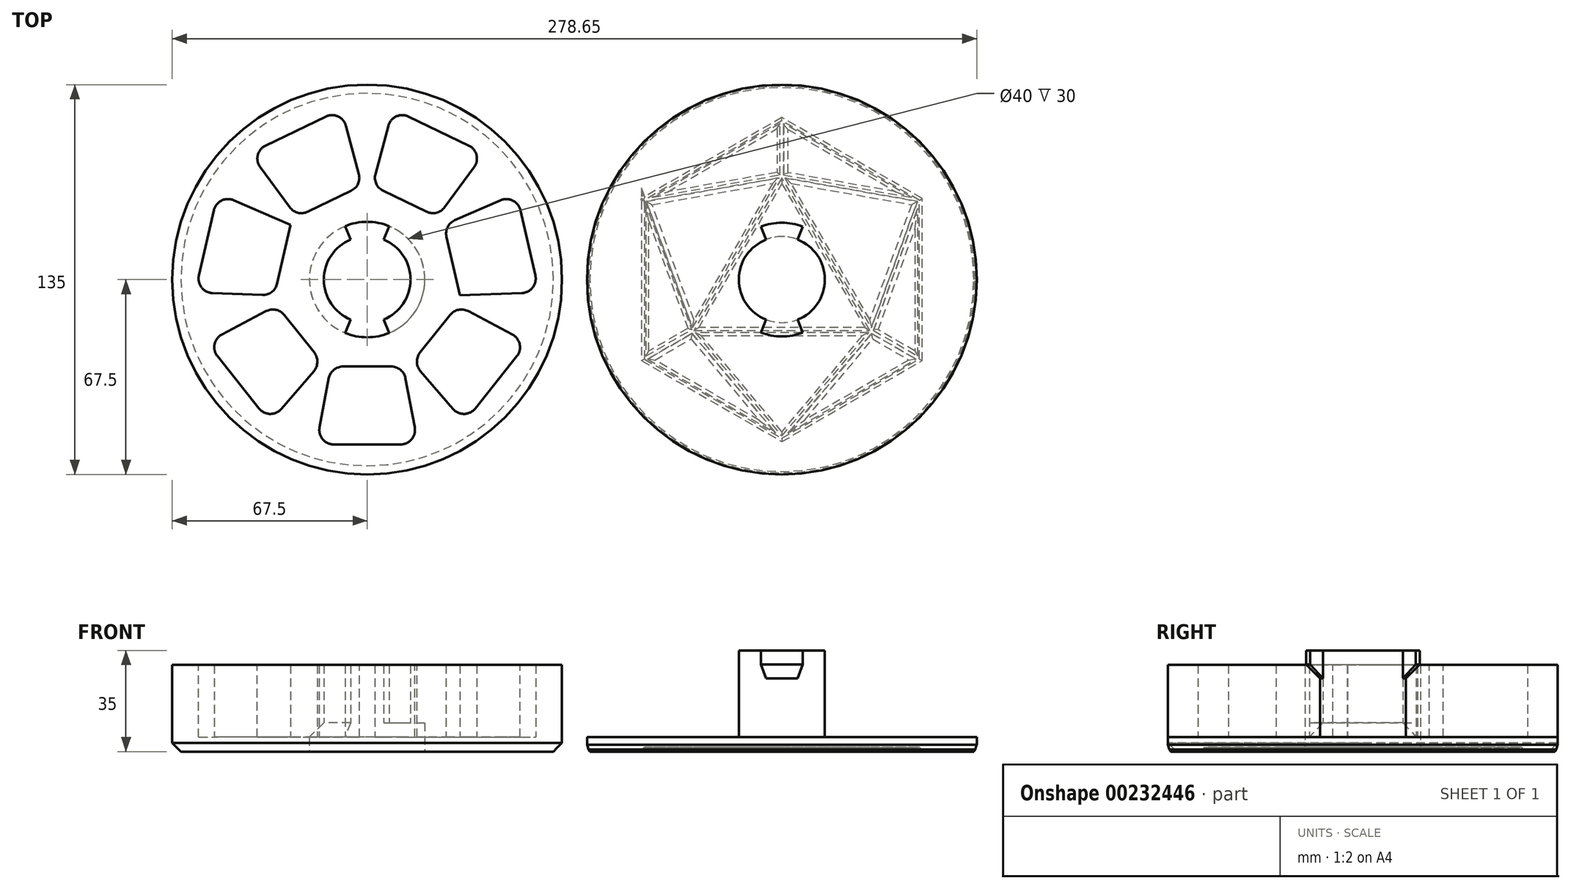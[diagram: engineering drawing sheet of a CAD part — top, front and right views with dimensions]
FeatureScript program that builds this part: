
annotation { "Feature Type Name" : "Feature", "Feature Type Description" : "" }
export const myFeature = defineFeature(function(context is Context, id is Id, definition is map)
    precondition{}
    {
        {
            var Q0;
            Q0=qCreatedBy(makeId("Top.planeOp"),FACE);
            var sketch = newSketch(context, id + "F0", { "sketchPlane" : qUnion([Q0])});
            skCircle(sketch, "E0.cCircle", {"center": v(0, 0) * mm, "radius": 63.39 * mm, "construction": true});
            skLineSegment(sketch, "E0.0", {"start": v(0, 63.39) * mm, "end": v(49.56, 39.52) * mm});
            skLineSegment(sketch, "E0.1", {"start": v(49.56, 39.52) * mm, "end": v(61.8, -14.1) * mm});
            skLineSegment(sketch, "E0.2", {"start": v(61.8, -14.1) * mm, "end": v(27.5, -57.1) * mm});
            skLineSegment(sketch, "E0.3", {"start": v(27.5, -57.1) * mm, "end": v(-27.5, -57.1) * mm});
            skLineSegment(sketch, "E0.4", {"start": v(-27.5, -57.1) * mm, "end": v(-61.8, -14.1) * mm});
            skLineSegment(sketch, "E0.5", {"start": v(-61.8, -14.1) * mm, "end": v(-49.56, 39.52) * mm});
            skLineSegment(sketch, "E0.6", {"start": v(-49.56, 39.52) * mm, "end": v(0, 63.39) * mm});
            skCircle(sketch, "E1.cCircle", {"center": v(0, 0) * mm, "radius": 33.42 * mm, "construction": true});
            skLineSegment(sketch, "E1.0", {"start": v(0, 33.42) * mm, "end": v(26.13, 20.84) * mm});
            skLineSegment(sketch, "E1.1", {"start": v(26.13, 20.84) * mm, "end": v(32.58, -7.44) * mm});
            skLineSegment(sketch, "E1.2", {"start": v(32.58, -7.44) * mm, "end": v(14.5, -30.1) * mm});
            skLineSegment(sketch, "E1.3", {"start": v(14.5, -30.1) * mm, "end": v(-14.5, -30.1) * mm});
            skLineSegment(sketch, "E1.4", {"start": v(-14.5, -30.1) * mm, "end": v(-32.58, -7.44) * mm});
            skLineSegment(sketch, "E1.5", {"start": v(-32.58, -7.44) * mm, "end": v(-26.13, 20.84) * mm});
            skLineSegment(sketch, "E1.6", {"start": v(-26.13, 20.84) * mm, "end": v(0, 33.42) * mm});
            skCircle(sketch, "E2", {"center": v(0, 0) * mm, "radius": 67.5 * mm});
            skCircle(sketch, "E3", {"center": v(0, 0) * mm, "radius": 15 * mm});
            skLineSegment(sketch, "E4", {"start": v(-26.13, 20.84) * mm, "end": v(-49.56, 39.52) * mm});
            skLineSegment(sketch, "E5", {"start": v(0, 33.42) * mm, "end": v(0, 63.39) * mm});
            skLineSegment(sketch, "E6", {"start": v(26.13, 20.84) * mm, "end": v(49.56, 39.52) * mm});
            skLineSegment(sketch, "E7", {"start": v(32.58, -7.44) * mm, "end": v(61.8, -14.1) * mm});
            skLineSegment(sketch, "E8", {"start": v(14.5, -30.1) * mm, "end": v(27.5, -57.1) * mm});
            skLineSegment(sketch, "E9", {"start": v(-14.5, -30.1) * mm, "end": v(-27.5, -57.1) * mm});
            skLineSegment(sketch, "E10", {"start": v(-61.8, -14.1) * mm, "end": v(-32.58, -7.44) * mm});
            skLineSegment(sketch, "E11", {"start": v(-26.57, 18.89) * mm, "end": v(-51.76, 29.88) * mm});
            skLineSegment(sketch, "E12", {"start": v(-24.33, 21.7) * mm, "end": v(-40.64, 43.81) * mm});
            skLineSegment(sketch, "E13", {"start": v(-1.8, 32.55) * mm, "end": v(-8.91, 59.1) * mm});
            skLineSegment(sketch, "E14", {"start": v(1.8, 32.55) * mm, "end": v(8.91, 59.1) * mm});
            skLineSegment(sketch, "E15", {"start": v(26.57, 18.89) * mm, "end": v(51.76, 29.88) * mm});
            skLineSegment(sketch, "E16", {"start": v(24.33, 21.7) * mm, "end": v(40.64, 43.81) * mm});
            skLineSegment(sketch, "E17", {"start": v(31.33, -9) * mm, "end": v(55.63, -21.84) * mm});
            skLineSegment(sketch, "E18", {"start": v(32.14, -5.49) * mm, "end": v(59.6, -4.46) * mm});
            skLineSegment(sketch, "E19", {"start": v(15.75, -28.55) * mm, "end": v(33.67, -49.37) * mm});
            skLineSegment(sketch, "E20", {"start": v(12.5, -30.1) * mm, "end": v(17.6, -57.1) * mm});
            skLineSegment(sketch, "E21", {"start": v(-12.5, -30.1) * mm, "end": v(-17.6, -57.1) * mm});
            skLineSegment(sketch, "E22", {"start": v(-15.75, -28.55) * mm, "end": v(-33.67, -49.37) * mm});
            skLineSegment(sketch, "E23", {"start": v(-31.33, -9) * mm, "end": v(-55.63, -21.84) * mm});
            skLineSegment(sketch, "E24", {"start": v(-32.14, -5.49) * mm, "end": v(-59.6, -4.46) * mm});
            skLineSegment(sketch, "E25", {"start": v(67.5, 0) * mm, "end": v(143.65, 0) * mm});
            skCircle(sketch, "E26", {"center": v(143.65, 0) * mm, "radius": 67.5 * mm});
            skCircle(sketch, "E27", {"center": v(0, 0) * mm, "radius": 20 * mm});
            skLineSegment(sketch, "E28", {"start": v(0, 0) * mm, "end": v(-7.65, 18.48) * mm});
            skLineSegment(sketch, "E29", {"start": v(0, 0) * mm, "end": v(7.65, 18.48) * mm});
            skLineSegment(sketch, "E30", {"start": v(0, 0) * mm, "end": v(-7.65, -18.48) * mm});
            skLineSegment(sketch, "E31", {"start": v(0, 0) * mm, "end": v(7.65, -18.48) * mm});
            skSolve(sketch);
        }
        {
            var Q0;
            {var subQ0=sQuery(id+"F0.wireOp",EDGE,"E28");var subQ1=sQuery(id+"F0.wireOp",EDGE,"E3");var subQ2=makeQuery(id+"F0.imprint","INTERSECT",VERTEX,{"derivedFrom":[subQ1,subQ0]});Q0=makeQuery(id+"F0.imprint","IMPRINT",FACE,{"disambiguationData":[TD([[makeQuery(id+"F0.imprint","IMPRINT",EDGE,{"disambiguationData":[TD([[subQ2,-1.0]])],"derivedFrom":subQ1}),-1.0]])]});}
            var Q1;
            {var subQ0=sQuery(id+"F0.wireOp",EDGE,"E29");var subQ1=sQuery(id+"F0.wireOp",EDGE,"E3");var subQ2=makeQuery(id+"F0.imprint","INTERSECT",VERTEX,{"derivedFrom":[subQ1,subQ0]});Q1=makeQuery(id+"F0.imprint","IMPRINT",FACE,{"disambiguationData":[TD([[makeQuery(id+"F0.imprint","IMPRINT",EDGE,{"disambiguationData":[TD([[subQ2,1.0]])],"derivedFrom":subQ1}),-1.0]])]});}
            var Q2;
            {var subQ0=sQuery(id+"F0.wireOp",EDGE,"E4");Q2=makeQuery(id+"F0.imprint","IMPRINT",FACE,{"disambiguationData":[TD([[makeQuery(id+"F0.imprint","IMPRINT",EDGE,{"derivedFrom":subQ0}),1.0]])]});}
            var Q3;
            {var subQ0=sQuery(id+"F0.wireOp",EDGE,"E4");Q3=makeQuery(id+"F0.imprint","IMPRINT",FACE,{"disambiguationData":[TD([[makeQuery(id+"F0.imprint","IMPRINT",EDGE,{"derivedFrom":subQ0}),-1.0]])]});}
            var Q4;
            Q4=makeQuery(id+"F0.imprint","IMPRINT",FACE,{"disambiguationData":[TD([[makeQuery(id+"F0.imprint","IMPRINT",EDGE,{"derivedFrom":sQuery(id+"F0.wireOp",EDGE,"E2")}),1.0]])]});
            var Q5;
            {var subQ0=sQuery(id+"F0.wireOp",EDGE,"E5");Q5=makeQuery(id+"F0.imprint","IMPRINT",FACE,{"disambiguationData":[TD([[makeQuery(id+"F0.imprint","IMPRINT",EDGE,{"derivedFrom":subQ0}),-1.0]])]});}
            var Q6;
            {var subQ0=sQuery(id+"F0.wireOp",EDGE,"E5");Q6=makeQuery(id+"F0.imprint","IMPRINT",FACE,{"disambiguationData":[TD([[makeQuery(id+"F0.imprint","IMPRINT",EDGE,{"derivedFrom":subQ0}),1.0]])]});}
            var Q7;
            {var subQ0=sQuery(id+"F0.wireOp",EDGE,"E6");Q7=makeQuery(id+"F0.imprint","IMPRINT",FACE,{"disambiguationData":[TD([[makeQuery(id+"F0.imprint","IMPRINT",EDGE,{"derivedFrom":subQ0}),1.0]])]});}
            var Q8;
            {var subQ0=sQuery(id+"F0.wireOp",EDGE,"E6");Q8=makeQuery(id+"F0.imprint","IMPRINT",FACE,{"disambiguationData":[TD([[makeQuery(id+"F0.imprint","IMPRINT",EDGE,{"derivedFrom":subQ0}),-1.0]])]});}
            var Q9;
            {var subQ0=sQuery(id+"F0.wireOp",EDGE,"E7");Q9=makeQuery(id+"F0.imprint","IMPRINT",FACE,{"disambiguationData":[TD([[makeQuery(id+"F0.imprint","IMPRINT",EDGE,{"derivedFrom":subQ0}),1.0]])]});}
            var Q10;
            {var subQ0=sQuery(id+"F0.wireOp",EDGE,"E7");Q10=makeQuery(id+"F0.imprint","IMPRINT",FACE,{"disambiguationData":[TD([[makeQuery(id+"F0.imprint","IMPRINT",EDGE,{"derivedFrom":subQ0}),-1.0]])]});}
            var Q11;
            {var subQ0=sQuery(id+"F0.wireOp",EDGE,"E8");Q11=makeQuery(id+"F0.imprint","IMPRINT",FACE,{"disambiguationData":[TD([[makeQuery(id+"F0.imprint","IMPRINT",EDGE,{"derivedFrom":subQ0}),1.0]])]});}
            var Q12;
            {var subQ0=sQuery(id+"F0.wireOp",EDGE,"E8");Q12=makeQuery(id+"F0.imprint","IMPRINT",FACE,{"disambiguationData":[TD([[makeQuery(id+"F0.imprint","IMPRINT",EDGE,{"derivedFrom":subQ0}),-1.0]])]});}
            var Q13;
            {var subQ0=sQuery(id+"F0.wireOp",EDGE,"E9");Q13=makeQuery(id+"F0.imprint","IMPRINT",FACE,{"disambiguationData":[TD([[makeQuery(id+"F0.imprint","IMPRINT",EDGE,{"derivedFrom":subQ0}),1.0]])]});}
            var Q14;
            {var subQ0=sQuery(id+"F0.wireOp",EDGE,"E9");Q14=makeQuery(id+"F0.imprint","IMPRINT",FACE,{"disambiguationData":[TD([[makeQuery(id+"F0.imprint","IMPRINT",EDGE,{"derivedFrom":subQ0}),-1.0]])]});}
            var Q15;
            {var subQ0=sQuery(id+"F0.wireOp",EDGE,"E10");Q15=makeQuery(id+"F0.imprint","IMPRINT",FACE,{"disambiguationData":[TD([[makeQuery(id+"F0.imprint","IMPRINT",EDGE,{"derivedFrom":subQ0}),-1.0]])]});}
            var Q16;
            {var subQ0=sQuery(id+"F0.wireOp",EDGE,"E10");Q16=makeQuery(id+"F0.imprint","IMPRINT",FACE,{"disambiguationData":[TD([[makeQuery(id+"F0.imprint","IMPRINT",EDGE,{"derivedFrom":subQ0}),1.0]])]});}
            var Q17;
            {var subQ1=sQuery(id+"F0.wireOp",EDGE,"E1.0");var subQ21=makeQuery(id+"F0.imprint","INTERSECT",VERTEX,{"derivedFrom":[subQ1,sQuery(id+"F0.wireOp",EDGE,"E14")]});Q17=makeQuery(id+"F0.imprint","IMPRINT",FACE,{"disambiguationData":[TD([[makeQuery(id+"F0.imprint","IMPRINT",EDGE,{"disambiguationData":[TD([[subQ21,-1.0]])],"derivedFrom":subQ1}),-1.0]])]});}
            extrude(context, id + "F1", {"entities" : qUnion([Q0, Q1, Q2, Q3, Q4, Q5, Q6, Q7, Q8, Q9, Q10, Q11, Q12, Q13, Q14, Q15, Q16, Q17]), "depth" : 25 * mm});
        }
        {
            var Q0;
            {var subQ0=sQuery(id+"F0.wireOp",EDGE,"E5");Q0=makeQuery(id+"F0.imprint","IMPRINT",FACE,{"disambiguationData":[TD([[makeQuery(id+"F0.imprint","IMPRINT",EDGE,{"derivedFrom":subQ0}),-1.0]])]});}
            var Q1;
            {var subQ0=sQuery(id+"F0.wireOp",EDGE,"E5");Q1=makeQuery(id+"F0.imprint","IMPRINT",FACE,{"disambiguationData":[TD([[makeQuery(id+"F0.imprint","IMPRINT",EDGE,{"derivedFrom":subQ0}),1.0]])]});}
            var Q2;
            {var subQ0=sQuery(id+"F0.wireOp",EDGE,"E4");Q2=makeQuery(id+"F0.imprint","IMPRINT",FACE,{"disambiguationData":[TD([[makeQuery(id+"F0.imprint","IMPRINT",EDGE,{"derivedFrom":subQ0}),-1.0]])]});}
            var Q3;
            {var subQ0=sQuery(id+"F0.wireOp",EDGE,"E4");Q3=makeQuery(id+"F0.imprint","IMPRINT",FACE,{"disambiguationData":[TD([[makeQuery(id+"F0.imprint","IMPRINT",EDGE,{"derivedFrom":subQ0}),1.0]])]});}
            var Q4;
            {var subQ0=sQuery(id+"F0.wireOp",EDGE,"E22");Q4=makeQuery(id+"F0.imprint","IMPRINT",FACE,{"disambiguationData":[TD([[makeQuery(id+"F0.imprint","IMPRINT",EDGE,{"derivedFrom":subQ0}),-1.0]])]});}
            var Q5;
            {var subQ0=sQuery(id+"F0.wireOp",EDGE,"E9");Q5=makeQuery(id+"F0.imprint","IMPRINT",FACE,{"disambiguationData":[TD([[makeQuery(id+"F0.imprint","IMPRINT",EDGE,{"derivedFrom":subQ0}),-1.0]])]});}
            var Q6;
            {var subQ0=sQuery(id+"F0.wireOp",EDGE,"E9");Q6=makeQuery(id+"F0.imprint","IMPRINT",FACE,{"disambiguationData":[TD([[makeQuery(id+"F0.imprint","IMPRINT",EDGE,{"derivedFrom":subQ0}),1.0]])]});}
            var Q7;
            {var subQ0=sQuery(id+"F0.wireOp",EDGE,"E20");Q7=makeQuery(id+"F0.imprint","IMPRINT",FACE,{"disambiguationData":[TD([[makeQuery(id+"F0.imprint","IMPRINT",EDGE,{"derivedFrom":subQ0}),-1.0]])]});}
            var Q8;
            {var subQ0=sQuery(id+"F0.wireOp",EDGE,"E8");Q8=makeQuery(id+"F0.imprint","IMPRINT",FACE,{"disambiguationData":[TD([[makeQuery(id+"F0.imprint","IMPRINT",EDGE,{"derivedFrom":subQ0}),-1.0]])]});}
            var Q9;
            {var subQ0=sQuery(id+"F0.wireOp",EDGE,"E8");Q9=makeQuery(id+"F0.imprint","IMPRINT",FACE,{"disambiguationData":[TD([[makeQuery(id+"F0.imprint","IMPRINT",EDGE,{"derivedFrom":subQ0}),1.0]])]});}
            var Q10;
            {var subQ0=sQuery(id+"F0.wireOp",EDGE,"E17");Q10=makeQuery(id+"F0.imprint","IMPRINT",FACE,{"disambiguationData":[TD([[makeQuery(id+"F0.imprint","IMPRINT",EDGE,{"derivedFrom":subQ0}),-1.0]])]});}
            var Q11;
            {var subQ0=sQuery(id+"F0.wireOp",EDGE,"E7");Q11=makeQuery(id+"F0.imprint","IMPRINT",FACE,{"disambiguationData":[TD([[makeQuery(id+"F0.imprint","IMPRINT",EDGE,{"derivedFrom":subQ0}),-1.0]])]});}
            var Q12;
            {var subQ0=sQuery(id+"F0.wireOp",EDGE,"E7");Q12=makeQuery(id+"F0.imprint","IMPRINT",FACE,{"disambiguationData":[TD([[makeQuery(id+"F0.imprint","IMPRINT",EDGE,{"derivedFrom":subQ0}),1.0]])]});}
            var Q13;
            {var subQ0=sQuery(id+"F0.wireOp",EDGE,"E15");Q13=makeQuery(id+"F0.imprint","IMPRINT",FACE,{"disambiguationData":[TD([[makeQuery(id+"F0.imprint","IMPRINT",EDGE,{"derivedFrom":subQ0}),-1.0]])]});}
            var Q14;
            {var subQ0=sQuery(id+"F0.wireOp",EDGE,"E6");Q14=makeQuery(id+"F0.imprint","IMPRINT",FACE,{"disambiguationData":[TD([[makeQuery(id+"F0.imprint","IMPRINT",EDGE,{"derivedFrom":subQ0}),-1.0]])]});}
            var Q15;
            {var subQ0=sQuery(id+"F0.wireOp",EDGE,"E6");Q15=makeQuery(id+"F0.imprint","IMPRINT",FACE,{"disambiguationData":[TD([[makeQuery(id+"F0.imprint","IMPRINT",EDGE,{"derivedFrom":subQ0}),1.0]])]});}
            var Q16;
            {var subQ0=sQuery(id+"F0.wireOp",EDGE,"E14");Q16=makeQuery(id+"F0.imprint","IMPRINT",FACE,{"disambiguationData":[TD([[makeQuery(id+"F0.imprint","IMPRINT",EDGE,{"derivedFrom":subQ0}),-1.0]])]});}
            var Q17;
            {var subQ0=sQuery(id+"F0.wireOp",EDGE,"E12");Q17=makeQuery(id+"F0.imprint","IMPRINT",FACE,{"disambiguationData":[TD([[makeQuery(id+"F0.imprint","IMPRINT",EDGE,{"derivedFrom":subQ0}),-1.0]])]});}
            var Q18;
            {var subQ0=sQuery(id+"F0.wireOp",EDGE,"E11");Q18=makeQuery(id+"F0.imprint","IMPRINT",FACE,{"disambiguationData":[TD([[makeQuery(id+"F0.imprint","IMPRINT",EDGE,{"derivedFrom":subQ0}),1.0]])]});}
            var Q19;
            {var subQ0=sQuery(id+"F0.wireOp",EDGE,"E10");Q19=makeQuery(id+"F0.imprint","IMPRINT",FACE,{"disambiguationData":[TD([[makeQuery(id+"F0.imprint","IMPRINT",EDGE,{"derivedFrom":subQ0}),1.0]])]});}
            var Q20;
            {var subQ0=sQuery(id+"F0.wireOp",EDGE,"E10");Q20=makeQuery(id+"F0.imprint","IMPRINT",FACE,{"disambiguationData":[TD([[makeQuery(id+"F0.imprint","IMPRINT",EDGE,{"derivedFrom":subQ0}),-1.0]])]});}
            var Q21;
            Q21=makeQuery(id+"F0.imprint","IMPRINT",FACE,{"disambiguationData":[TD([[makeQuery(id+"F0.imprint","IMPRINT",EDGE,{"derivedFrom":sQuery(id+"F0.wireOp",EDGE,"E2")}),1.0]])]});
            var Q22;
            Q22=makeQuery(id+"F0.imprint","IMPRINT",FACE,{"disambiguationData":[TD([[makeQuery(id+"F0.imprint","IMPRINT",EDGE,{"derivedFrom":sQuery(id+"F0.wireOp",EDGE,"E26")}),1.0]])]});
            var Q23;
            Q23=makeQuery(id+"F0.imprint","IMPRINT",FACE,{"disambiguationData":[TD([[makeQuery(id+"F0.imprint","IMPRINT",EDGE,{"derivedFrom":sQuery(id+"F0.wireOp",EDGE,"E27")}),-1.0]])]});
            extrude(context, id + "F2", {"entities" : qUnion([Q0, Q1, Q2, Q3, Q4, Q5, Q6, Q7, Q8, Q9, Q10, Q11, Q12, Q13, Q14, Q15, Q16, Q17, Q18, Q19, Q20, Q21, Q22, Q23]), "operationType" : NewBodyOperationType.ADD, "oppositeDirection" : true, "depth" : 5 * mm});
        }
        {
            var Q0;
            {var subQ0=sQuery(id+"F0.wireOp",EDGE,"E28");var subQ1=sQuery(id+"F0.wireOp",EDGE,"E30");var subQ2=sQuery(id+"F0.wireOp",EDGE,"E27");var subQ3=sQuery(id+"F0.wireOp",EDGE,"E31");var subQ4=sQuery(id+"F0.wireOp",EDGE,"E29");var subQ5=sQuery(id+"F0.wireOp",EDGE,"E3");Q0=makeQuery(id+"F2.boolean.opBoolean","SPLIT",FACE,{"disambiguationData":[TD([makeQuery(id+"F1.opExtrude","SWEPT_FACE",FACE,{"disambiguationData":[OSD([subQ0])]})])],"derivedFrom":makeQuery(id+"F1.opExtrude","CAP_FACE",FACE,{"disambiguationData":[OSD([sQuery(id+"F0.wireOp",EDGE,"E0.0"),sQuery(id+"F0.wireOp",EDGE,"E0.1"),sQuery(id+"F0.wireOp",EDGE,"E0.2"),sQuery(id+"F0.wireOp",EDGE,"E0.3"),sQuery(id+"F0.wireOp",EDGE,"E0.4"),sQuery(id+"F0.wireOp",EDGE,"E0.5"),sQuery(id+"F0.wireOp",EDGE,"E0.6"),sQuery(id+"F0.wireOp",EDGE,"E1.0"),sQuery(id+"F0.wireOp",EDGE,"E1.1"),sQuery(id+"F0.wireOp",EDGE,"E1.2"),sQuery(id+"F0.wireOp",EDGE,"E1.3"),sQuery(id+"F0.wireOp",EDGE,"E1.4"),sQuery(id+"F0.wireOp",EDGE,"E1.5"),sQuery(id+"F0.wireOp",EDGE,"E1.6"),sQuery(id+"F0.wireOp",EDGE,"E2"),subQ5,sQuery(id+"F0.wireOp",EDGE,"E11"),sQuery(id+"F0.wireOp",EDGE,"E12"),sQuery(id+"F0.wireOp",EDGE,"E13"),sQuery(id+"F0.wireOp",EDGE,"E14"),sQuery(id+"F0.wireOp",EDGE,"E15"),sQuery(id+"F0.wireOp",EDGE,"E16"),sQuery(id+"F0.wireOp",EDGE,"E17"),sQuery(id+"F0.wireOp",EDGE,"E18"),sQuery(id+"F0.wireOp",EDGE,"E19"),sQuery(id+"F0.wireOp",EDGE,"E20"),sQuery(id+"F0.wireOp",EDGE,"E21"),sQuery(id+"F0.wireOp",EDGE,"E22"),sQuery(id+"F0.wireOp",EDGE,"E23"),sQuery(id+"F0.wireOp",EDGE,"E24"),subQ2,subQ0,subQ4,subQ1,subQ3])],"isStart":true})});}
            var Q1;
            {var subQ0=sQuery(id+"F0.wireOp",EDGE,"E29");var subQ1=sQuery(id+"F0.wireOp",EDGE,"E30");var subQ2=sQuery(id+"F0.wireOp",EDGE,"E27");var subQ3=sQuery(id+"F0.wireOp",EDGE,"E31");var subQ4=sQuery(id+"F0.wireOp",EDGE,"E3");var subQ5=sQuery(id+"F0.wireOp",EDGE,"E28");Q1=makeQuery(id+"F2.boolean.opBoolean","SPLIT",FACE,{"disambiguationData":[TD([makeQuery(id+"F1.opExtrude","SWEPT_FACE",FACE,{"disambiguationData":[OSD([subQ0])]})])],"derivedFrom":makeQuery(id+"F1.opExtrude","CAP_FACE",FACE,{"disambiguationData":[OSD([sQuery(id+"F0.wireOp",EDGE,"E0.0"),sQuery(id+"F0.wireOp",EDGE,"E0.1"),sQuery(id+"F0.wireOp",EDGE,"E0.2"),sQuery(id+"F0.wireOp",EDGE,"E0.3"),sQuery(id+"F0.wireOp",EDGE,"E0.4"),sQuery(id+"F0.wireOp",EDGE,"E0.5"),sQuery(id+"F0.wireOp",EDGE,"E0.6"),sQuery(id+"F0.wireOp",EDGE,"E1.0"),sQuery(id+"F0.wireOp",EDGE,"E1.1"),sQuery(id+"F0.wireOp",EDGE,"E1.2"),sQuery(id+"F0.wireOp",EDGE,"E1.3"),sQuery(id+"F0.wireOp",EDGE,"E1.4"),sQuery(id+"F0.wireOp",EDGE,"E1.5"),sQuery(id+"F0.wireOp",EDGE,"E1.6"),sQuery(id+"F0.wireOp",EDGE,"E2"),subQ4,sQuery(id+"F0.wireOp",EDGE,"E11"),sQuery(id+"F0.wireOp",EDGE,"E12"),sQuery(id+"F0.wireOp",EDGE,"E13"),sQuery(id+"F0.wireOp",EDGE,"E14"),sQuery(id+"F0.wireOp",EDGE,"E15"),sQuery(id+"F0.wireOp",EDGE,"E16"),sQuery(id+"F0.wireOp",EDGE,"E17"),sQuery(id+"F0.wireOp",EDGE,"E18"),sQuery(id+"F0.wireOp",EDGE,"E19"),sQuery(id+"F0.wireOp",EDGE,"E20"),sQuery(id+"F0.wireOp",EDGE,"E21"),sQuery(id+"F0.wireOp",EDGE,"E22"),sQuery(id+"F0.wireOp",EDGE,"E23"),sQuery(id+"F0.wireOp",EDGE,"E24"),subQ2,subQ5,subQ0,subQ1,subQ3])],"isStart":true})});}
            extrude(context, id + "F3", {"entities" : qUnion([Q0, Q1]), "oppositeDirection" : true, "depth" : 5 * mm});
        }
        {
            var Q0;
            {var subQ0=sQuery(id+"F0.wireOp",EDGE,"E28");var subQ1=sQuery(id+"F0.wireOp",EDGE,"E30");var subQ2=sQuery(id+"F0.wireOp",EDGE,"E27");var subQ3=sQuery(id+"F0.wireOp",EDGE,"E31");var subQ4=sQuery(id+"F0.wireOp",EDGE,"E29");var subQ5=sQuery(id+"F0.wireOp",EDGE,"E3");var subQ6=sQuery(id+"F0.wireOp",EDGE,"E24");var subQ7=sQuery(id+"F0.wireOp",EDGE,"E23");var subQ8=sQuery(id+"F0.wireOp",EDGE,"E22");var subQ9=sQuery(id+"F0.wireOp",EDGE,"E21");var subQ10=sQuery(id+"F0.wireOp",EDGE,"E20");var subQ11=sQuery(id+"F0.wireOp",EDGE,"E19");var subQ12=sQuery(id+"F0.wireOp",EDGE,"E18");var subQ13=sQuery(id+"F0.wireOp",EDGE,"E17");var subQ14=sQuery(id+"F0.wireOp",EDGE,"E16");var subQ15=sQuery(id+"F0.wireOp",EDGE,"E15");var subQ16=sQuery(id+"F0.wireOp",EDGE,"E14");var subQ17=sQuery(id+"F0.wireOp",EDGE,"E13");var subQ18=sQuery(id+"F0.wireOp",EDGE,"E12");var subQ19=sQuery(id+"F0.wireOp",EDGE,"E11");var subQ20=sQuery(id+"F0.wireOp",EDGE,"E2");var subQ21=sQuery(id+"F0.wireOp",EDGE,"E1.6");var subQ22=sQuery(id+"F0.wireOp",EDGE,"E1.5");var subQ23=sQuery(id+"F0.wireOp",EDGE,"E1.4");var subQ24=sQuery(id+"F0.wireOp",EDGE,"E1.3");var subQ25=sQuery(id+"F0.wireOp",EDGE,"E1.2");var subQ26=sQuery(id+"F0.wireOp",EDGE,"E1.1");var subQ27=sQuery(id+"F0.wireOp",EDGE,"E1.0");var subQ28=sQuery(id+"F0.wireOp",EDGE,"E0.6");var subQ29=sQuery(id+"F0.wireOp",EDGE,"E0.5");var subQ30=sQuery(id+"F0.wireOp",EDGE,"E0.4");var subQ31=sQuery(id+"F0.wireOp",EDGE,"E0.3");var subQ32=sQuery(id+"F0.wireOp",EDGE,"E0.2");var subQ33=sQuery(id+"F0.wireOp",EDGE,"E0.1");var subQ34=sQuery(id+"F0.wireOp",EDGE,"E0.0");Q0=makeQuery(id+"F3.opExtrude","SWEPT_BODY",BODY,{"disambiguationData":[OSD([subQ34,subQ33,subQ32,subQ31,subQ30,subQ29,subQ28,subQ27,subQ26,subQ25,subQ24,subQ23,subQ22,subQ21,subQ20,subQ5,subQ19,subQ18,subQ17,subQ16,subQ15,subQ14,subQ13,subQ12,subQ11,subQ10,subQ9,subQ8,subQ7,subQ6,subQ2,subQ0,subQ4,subQ1,subQ3]),TDD([makeQuery(id+"F2.boolean.opBoolean","SPLIT",FACE,{"disambiguationData":[TD([makeQuery(id+"F1.opExtrude","SWEPT_FACE",FACE,{"disambiguationData":[OSD([subQ0])]})])],"derivedFrom":makeQuery(id+"F1.opExtrude","CAP_FACE",FACE,{"disambiguationData":[OSD([subQ34,subQ33,subQ32,subQ31,subQ30,subQ29,subQ28,subQ27,subQ26,subQ25,subQ24,subQ23,subQ22,subQ21,subQ20,subQ5,subQ19,subQ18,subQ17,subQ16,subQ15,subQ14,subQ13,subQ12,subQ11,subQ10,subQ9,subQ8,subQ7,subQ6,subQ2,subQ0,subQ4,subQ1,subQ3])],"isStart":true})})])]});}
            var Q1;
            {var subQ0=sQuery(id+"F0.wireOp",EDGE,"E29");var subQ1=sQuery(id+"F0.wireOp",EDGE,"E30");var subQ2=sQuery(id+"F0.wireOp",EDGE,"E27");var subQ3=sQuery(id+"F0.wireOp",EDGE,"E31");var subQ4=sQuery(id+"F0.wireOp",EDGE,"E3");var subQ5=sQuery(id+"F0.wireOp",EDGE,"E28");var subQ6=sQuery(id+"F0.wireOp",EDGE,"E24");var subQ7=sQuery(id+"F0.wireOp",EDGE,"E23");var subQ8=sQuery(id+"F0.wireOp",EDGE,"E22");var subQ9=sQuery(id+"F0.wireOp",EDGE,"E21");var subQ10=sQuery(id+"F0.wireOp",EDGE,"E20");var subQ11=sQuery(id+"F0.wireOp",EDGE,"E19");var subQ12=sQuery(id+"F0.wireOp",EDGE,"E18");var subQ13=sQuery(id+"F0.wireOp",EDGE,"E17");var subQ14=sQuery(id+"F0.wireOp",EDGE,"E16");var subQ15=sQuery(id+"F0.wireOp",EDGE,"E15");var subQ16=sQuery(id+"F0.wireOp",EDGE,"E14");var subQ17=sQuery(id+"F0.wireOp",EDGE,"E13");var subQ18=sQuery(id+"F0.wireOp",EDGE,"E12");var subQ19=sQuery(id+"F0.wireOp",EDGE,"E11");var subQ20=sQuery(id+"F0.wireOp",EDGE,"E2");var subQ21=sQuery(id+"F0.wireOp",EDGE,"E1.6");var subQ22=sQuery(id+"F0.wireOp",EDGE,"E1.5");var subQ23=sQuery(id+"F0.wireOp",EDGE,"E1.4");var subQ24=sQuery(id+"F0.wireOp",EDGE,"E1.3");var subQ25=sQuery(id+"F0.wireOp",EDGE,"E1.2");var subQ26=sQuery(id+"F0.wireOp",EDGE,"E1.1");var subQ27=sQuery(id+"F0.wireOp",EDGE,"E1.0");var subQ28=sQuery(id+"F0.wireOp",EDGE,"E0.6");var subQ29=sQuery(id+"F0.wireOp",EDGE,"E0.5");var subQ30=sQuery(id+"F0.wireOp",EDGE,"E0.4");var subQ31=sQuery(id+"F0.wireOp",EDGE,"E0.3");var subQ32=sQuery(id+"F0.wireOp",EDGE,"E0.2");var subQ33=sQuery(id+"F0.wireOp",EDGE,"E0.1");var subQ34=sQuery(id+"F0.wireOp",EDGE,"E0.0");Q1=makeQuery(id+"F3.opExtrude","SWEPT_BODY",BODY,{"disambiguationData":[OSD([subQ34,subQ33,subQ32,subQ31,subQ30,subQ29,subQ28,subQ27,subQ26,subQ25,subQ24,subQ23,subQ22,subQ21,subQ20,subQ4,subQ19,subQ18,subQ17,subQ16,subQ15,subQ14,subQ13,subQ12,subQ11,subQ10,subQ9,subQ8,subQ7,subQ6,subQ2,subQ5,subQ0,subQ1,subQ3]),TDD([makeQuery(id+"F2.boolean.opBoolean","SPLIT",FACE,{"disambiguationData":[TD([makeQuery(id+"F1.opExtrude","SWEPT_FACE",FACE,{"disambiguationData":[OSD([subQ0])]})])],"derivedFrom":makeQuery(id+"F1.opExtrude","CAP_FACE",FACE,{"disambiguationData":[OSD([subQ34,subQ33,subQ32,subQ31,subQ30,subQ29,subQ28,subQ27,subQ26,subQ25,subQ24,subQ23,subQ22,subQ21,subQ20,subQ4,subQ19,subQ18,subQ17,subQ16,subQ15,subQ14,subQ13,subQ12,subQ11,subQ10,subQ9,subQ8,subQ7,subQ6,subQ2,subQ5,subQ0,subQ1,subQ3])],"isStart":true})})])]});}
            var Q2;
            Q2=makeQuery(id+"F1.opExtrude","SWEPT_BODY",BODY,{"disambiguationData":[OSD([sQuery(id+"F0.wireOp",EDGE,"E0.0"),sQuery(id+"F0.wireOp",EDGE,"E0.1"),sQuery(id+"F0.wireOp",EDGE,"E0.2"),sQuery(id+"F0.wireOp",EDGE,"E0.3"),sQuery(id+"F0.wireOp",EDGE,"E0.4"),sQuery(id+"F0.wireOp",EDGE,"E0.5"),sQuery(id+"F0.wireOp",EDGE,"E0.6"),sQuery(id+"F0.wireOp",EDGE,"E1.0"),sQuery(id+"F0.wireOp",EDGE,"E1.1"),sQuery(id+"F0.wireOp",EDGE,"E1.2"),sQuery(id+"F0.wireOp",EDGE,"E1.3"),sQuery(id+"F0.wireOp",EDGE,"E1.4"),sQuery(id+"F0.wireOp",EDGE,"E1.5"),sQuery(id+"F0.wireOp",EDGE,"E1.6"),sQuery(id+"F0.wireOp",EDGE,"E2"),sQuery(id+"F0.wireOp",EDGE,"E3"),sQuery(id+"F0.wireOp",EDGE,"E11"),sQuery(id+"F0.wireOp",EDGE,"E12"),sQuery(id+"F0.wireOp",EDGE,"E13"),sQuery(id+"F0.wireOp",EDGE,"E14"),sQuery(id+"F0.wireOp",EDGE,"E15"),sQuery(id+"F0.wireOp",EDGE,"E16"),sQuery(id+"F0.wireOp",EDGE,"E17"),sQuery(id+"F0.wireOp",EDGE,"E18"),sQuery(id+"F0.wireOp",EDGE,"E19"),sQuery(id+"F0.wireOp",EDGE,"E20"),sQuery(id+"F0.wireOp",EDGE,"E21"),sQuery(id+"F0.wireOp",EDGE,"E22"),sQuery(id+"F0.wireOp",EDGE,"E23"),sQuery(id+"F0.wireOp",EDGE,"E24"),sQuery(id+"F0.wireOp",EDGE,"E27"),sQuery(id+"F0.wireOp",EDGE,"E28"),sQuery(id+"F0.wireOp",EDGE,"E29"),sQuery(id+"F0.wireOp",EDGE,"E30"),sQuery(id+"F0.wireOp",EDGE,"E31")])]});
            booleanBodies(context, id + "F4", {"operationType" : BooleanOperationType.SUBTRACTION, "tools" : qUnion([Q0, Q1]), "targets" : qUnion([Q2])});
        }
        {
            var Q0;
            Q0=makeQuery(id+"F0.imprint","IMPRINT",FACE,{"disambiguationData":[TD([[makeQuery(id+"F0.imprint","IMPRINT",EDGE,{"derivedFrom":sQuery(id+"F0.wireOp",EDGE,"E26")}),1.0]])]});
            var sketch = newSketch(context, id + "F5", { "sketchPlane" : qUnion([Q0])});
            skCircle(sketch, "E32", {"center": v(143.65, 0) * mm, "radius": 14.9 * mm});
            skSolve(sketch);
        }
        {
            var Q0;
            Q0=makeQuery(id+"F5.imprint","IMPRINT",FACE,{"disambiguationData":[TD([[makeQuery(id+"F5.imprint","IMPRINT",EDGE,{"derivedFrom":sQuery(id+"F5.wireOp",EDGE,"E32")}),1.0]])]});
            extrude(context, id + "F6", {"entities" : qUnion([Q0]), "operationType" : NewBodyOperationType.ADD, "depth" : 20.2 * mm});
        }
        {
            var Q0;
            Q0=makeQuery(id+"F6.opExtrude","CAP_FACE",FACE,{"disambiguationData":[OSD([sQuery(id+"F5.wireOp",EDGE,"E32")])],"isStart":false});
            var sketch = newSketch(context, id + "F7", { "sketchPlane" : qUnion([Q0])});
            skCircle(sketch, "E33", {"center": v(143.65, 0) * mm, "radius": 19.7 * mm});
            skLineSegment(sketch, "E34", {"start": v(143.65, 0) * mm, "end": v(136.43, 18.33) * mm});
            skLineSegment(sketch, "E35", {"start": v(143.65, 0) * mm, "end": v(150.87, -18.33) * mm});
            skLineSegment(sketch, "E36", {"start": v(143.65, 0) * mm, "end": v(143.65, 19.7) * mm});
            skLineSegment(sketch, "E37", {"start": v(143.65, 0) * mm, "end": v(150.87, 18.33) * mm});
            skLineSegment(sketch, "E38", {"start": v(143.65, 0) * mm, "end": v(136.43, -18.33) * mm});
            skSolve(sketch);
        }
        {
            var Q0;
            {var subQ1=sQuery(id+"F7.wireOp",EDGE,"E34");var subQ3=makeQuery(id+"F6.opExtrude","CAP_EDGE",EDGE,{"disambiguationData":[OSD([sQuery(id+"F5.wireOp",EDGE,"E32")])],"isStart":false});var subQ4=makeQuery(id+"F7.imprint","INTERSECT",VERTEX,{"derivedFrom":[subQ3,subQ1]});Q0=makeQuery(id+"F7.imprint","IMPRINT",FACE,{"disambiguationData":[TD([[makeQuery(id+"F7.imprint","IMPRINT",EDGE,{"disambiguationData":[TD([[subQ4,1.0]])],"derivedFrom":subQ3}),1.0]])]});}
            var Q1;
            {var subQ1=sQuery(id+"F7.wireOp",EDGE,"E36");var subQ3=makeQuery(id+"F6.opExtrude","CAP_EDGE",EDGE,{"disambiguationData":[OSD([sQuery(id+"F5.wireOp",EDGE,"E32")])],"isStart":false});var subQ4=makeQuery(id+"F7.imprint","INTERSECT",VERTEX,{"derivedFrom":[subQ3,subQ1]});Q1=makeQuery(id+"F7.imprint","IMPRINT",FACE,{"disambiguationData":[TD([[makeQuery(id+"F7.imprint","IMPRINT",EDGE,{"disambiguationData":[TD([[subQ4,1.0]])],"derivedFrom":subQ3}),1.0]])]});}
            var Q2;
            {var subQ0=sQuery(id+"F7.wireOp",EDGE,"E34");var subQ1=sQuery(id+"F7.wireOp",EDGE,"E33");var subQ2=makeQuery(id+"F7.imprint","INTERSECT",VERTEX,{"derivedFrom":[subQ1,subQ0]});Q2=makeQuery(id+"F7.imprint","IMPRINT",FACE,{"disambiguationData":[TD([[makeQuery(id+"F7.imprint","IMPRINT",EDGE,{"disambiguationData":[TD([[subQ2,1.0]])],"derivedFrom":subQ1}),1.0]])]});}
            var Q3;
            {var subQ0=sQuery(id+"F7.wireOp",EDGE,"E36");var subQ1=sQuery(id+"F7.wireOp",EDGE,"E33");var subQ2=makeQuery(id+"F7.imprint","INTERSECT",VERTEX,{"derivedFrom":[subQ1,subQ0]});Q3=makeQuery(id+"F7.imprint","IMPRINT",FACE,{"disambiguationData":[TD([[makeQuery(id+"F7.imprint","IMPRINT",EDGE,{"disambiguationData":[TD([[subQ2,1.0]])],"derivedFrom":subQ1}),1.0]])]});}
            var Q4;
            {var subQ1=sQuery(id+"F7.wireOp",EDGE,"E34");var subQ3=makeQuery(id+"F6.opExtrude","CAP_EDGE",EDGE,{"disambiguationData":[OSD([sQuery(id+"F5.wireOp",EDGE,"E32")])],"isStart":false});var subQ4=makeQuery(id+"F7.imprint","INTERSECT",VERTEX,{"derivedFrom":[subQ3,subQ1]});Q4=makeQuery(id+"F7.imprint","IMPRINT",FACE,{"disambiguationData":[TD([[makeQuery(id+"F7.imprint","IMPRINT",EDGE,{"disambiguationData":[TD([[subQ4,-1.0]])],"derivedFrom":subQ3}),1.0]])]});}
            var Q5;
            {var subQ1=sQuery(id+"F7.wireOp",EDGE,"E35");var subQ3=makeQuery(id+"F6.opExtrude","CAP_EDGE",EDGE,{"disambiguationData":[OSD([sQuery(id+"F5.wireOp",EDGE,"E32")])],"isStart":false});var subQ4=makeQuery(id+"F7.imprint","INTERSECT",VERTEX,{"derivedFrom":[subQ3,subQ1]});Q5=makeQuery(id+"F7.imprint","IMPRINT",FACE,{"disambiguationData":[TD([[makeQuery(id+"F7.imprint","IMPRINT",EDGE,{"disambiguationData":[TD([[subQ4,-1.0]])],"derivedFrom":subQ3}),1.0]])]});}
            var Q6;
            {var subQ0=sQuery(id+"F7.wireOp",EDGE,"E35");var subQ1=sQuery(id+"F7.wireOp",EDGE,"E33");var subQ2=makeQuery(id+"F7.imprint","INTERSECT",VERTEX,{"derivedFrom":[subQ1,subQ0]});Q6=makeQuery(id+"F7.imprint","IMPRINT",FACE,{"disambiguationData":[TD([[makeQuery(id+"F7.imprint","IMPRINT",EDGE,{"disambiguationData":[TD([[subQ2,1.0]])],"derivedFrom":subQ1}),1.0]])]});}
            var Q7;
            {var subQ1=sQuery(id+"F7.wireOp",EDGE,"E35");var subQ3=makeQuery(id+"F6.opExtrude","CAP_EDGE",EDGE,{"disambiguationData":[OSD([sQuery(id+"F5.wireOp",EDGE,"E32")])],"isStart":false});var subQ4=makeQuery(id+"F7.imprint","INTERSECT",VERTEX,{"derivedFrom":[subQ3,subQ1]});Q7=makeQuery(id+"F7.imprint","IMPRINT",FACE,{"disambiguationData":[TD([[makeQuery(id+"F7.imprint","IMPRINT",EDGE,{"disambiguationData":[TD([[subQ4,1.0]])],"derivedFrom":subQ3}),1.0]])]});}
            extrude(context, id + "F8", {"entities" : qUnion([Q0, Q1, Q2, Q3, Q4, Q5, Q6, Q7]), "operationType" : NewBodyOperationType.ADD, "depth" : 9.8 * mm});
        }
        {
            var Q0;
            {var subQ0=sQuery(id+"F0.wireOp",EDGE,"E28");var subQ1=sQuery(id+"F0.wireOp",EDGE,"E27");Q0=makeQuery(id+"F4.opBoolean","COPY",EDGE,{"derivedFrom":makeQuery(id+"F3.opExtrude","CAP_EDGE",EDGE,{"disambiguationData":[OSD([subQ1]),TDD([makeQuery(id+"F2.boolean.opBoolean","SPLIT",EDGE,{"disambiguationData":[TD([makeQuery(id+"F1.opExtrude","SWEPT_FACE",FACE,{"disambiguationData":[OSD([subQ0])]})])],"derivedFrom":makeQuery(id+"F2.opExtrude","CAP_EDGE",EDGE,{"disambiguationData":[OSD([subQ1])],"isStart":true})})])],"isStart":false})});}
            var Q1;
            {var subQ0=sQuery(id+"F0.wireOp",EDGE,"E29");var subQ2=sQuery(id+"F0.wireOp",EDGE,"E27");Q1=makeQuery(id+"F4.opBoolean","COPY",EDGE,{"derivedFrom":makeQuery(id+"F3.opExtrude","CAP_EDGE",EDGE,{"disambiguationData":[OSD([subQ2]),TDD([makeQuery(id+"F2.boolean.opBoolean","SPLIT",EDGE,{"disambiguationData":[TD([makeQuery(id+"F1.opExtrude","SWEPT_FACE",FACE,{"disambiguationData":[OSD([subQ0])]})])],"derivedFrom":makeQuery(id+"F2.opExtrude","CAP_EDGE",EDGE,{"disambiguationData":[OSD([subQ2])],"isStart":true})})])],"isStart":false})});}
            chamfer(context, id + "F9", {"entities" : qUnion([Q0, Q1]), "width" : 5 * mm, "tangentPropagation" : true});
        }
        {
            var Q0;
            {var subQ0=sQuery(id+"F7.wireOp",EDGE,"E33");Q0=makeQuery(id+"F8.opExtrude","CAP_EDGE",EDGE,{"disambiguationData":[OSD([subQ0]),TDD([makeQuery(id+"F7.imprint","IMPRINT",EDGE,{"disambiguationData":[TD([[makeQuery(id+"F7.imprint","INTERSECT",VERTEX,{"derivedFrom":[subQ0,sQuery(id+"F7.wireOp",EDGE,"E35")]}),1.0]])],"derivedFrom":subQ0})])],"isStart":true});}
            var Q1;
            {var subQ0=sQuery(id+"F7.wireOp",EDGE,"E33");var subQ1=makeQuery(id+"F7.imprint","INTERSECT",VERTEX,{"derivedFrom":[subQ0,sQuery(id+"F7.wireOp",EDGE,"E36")]});Q1=makeQuery(id+"F8.opExtrude","CAP_EDGE",EDGE,{"disambiguationData":[OSD([subQ0]),TDD([makeQuery(id+"F7.imprint","IMPRINT",EDGE,{"disambiguationData":[TD([[subQ1,1.0]])],"derivedFrom":subQ0}),makeQuery(id+"F7.imprint","IMPRINT",EDGE,{"disambiguationData":[TD([[makeQuery(id+"F7.imprint","INTERSECT",VERTEX,{"derivedFrom":[subQ0,sQuery(id+"F7.wireOp",EDGE,"E34")]}),1.0]])],"derivedFrom":subQ0})])],"isStart":true});}
            chamfer(context, id + "F10", {"entities" : qUnion([Q0, Q1]), "width" : 5 * mm, "tangentPropagation" : true});
        }
        {
            var Q0;
            Q0=makeQuery(id+"F2.opExtrude","CAP_FACE",FACE,{"disambiguationData":[OSD([sQuery(id+"F0.wireOp",EDGE,"E26")])],"isStart":false});
            var sketch = newSketch(context, id + "F11", { "sketchPlane" : qUnion([Q0])});
            skCircle(sketch, "E39", {"center": v(143.65, 0) * mm, "radius": 67.5 * mm});
            skPoint(sketch, "E39.first.point", {"position": v(117.08, 62.05) * mm});
            skPoint(sketch, "E39.second.point", {"position": v(211.12, -2.05) * mm});
            skPoint(sketch, "E39.third.point", {"position": v(82.88, -29.37) * mm});
            skCircle(sketch, "E40", {"center": v(143.65, 0) * mm, "radius": 55 * mm});
            skLineSegment(sketch, "E41.0", {"start": v(143.65, -35.9) * mm, "end": v(112.56, 17.95) * mm});
            skLineSegment(sketch, "E41.1", {"start": v(112.56, 17.95) * mm, "end": v(174.74, 17.95) * mm});
            skLineSegment(sketch, "E41.2", {"start": v(174.74, 17.95) * mm, "end": v(143.65, -35.9) * mm});
            skLineSegment(sketch, "E42", {"start": v(112.56, 17.95) * mm, "end": v(143.65, 55) * mm});
            skLineSegment(sketch, "E43", {"start": v(143.65, 55) * mm, "end": v(174.74, 17.95) * mm});
            skLineSegment(sketch, "E44", {"start": v(174.74, 17.95) * mm, "end": v(191.28, -27.5) * mm});
            skLineSegment(sketch, "E45", {"start": v(191.28, -27.5) * mm, "end": v(143.65, -35.9) * mm});
            skLineSegment(sketch, "E46", {"start": v(143.65, -35.9) * mm, "end": v(96.02, -27.5) * mm});
            skLineSegment(sketch, "E47", {"start": v(96.02, -27.5) * mm, "end": v(112.56, 17.95) * mm});
            skLineSegment(sketch, "E48", {"start": v(112.56, 17.95) * mm, "end": v(96.02, 27.5) * mm});
            skLineSegment(sketch, "E49", {"start": v(174.74, 17.95) * mm, "end": v(191.28, 27.5) * mm});
            skLineSegment(sketch, "E50", {"start": v(143.65, -35.9) * mm, "end": v(143.65, -55) * mm});
            skLineSegment(sketch, "E51", {"start": v(96.02, 27.5) * mm, "end": v(143.65, 55) * mm});
            skLineSegment(sketch, "E52", {"start": v(143.65, 55) * mm, "end": v(191.28, 27.5) * mm});
            skLineSegment(sketch, "E53", {"start": v(191.28, 27.5) * mm, "end": v(191.28, -27.5) * mm});
            skLineSegment(sketch, "E54", {"start": v(191.28, -27.5) * mm, "end": v(143.65, -55) * mm});
            skLineSegment(sketch, "E55", {"start": v(143.65, -55) * mm, "end": v(96.02, -27.5) * mm});
            skLineSegment(sketch, "E56", {"start": v(96.02, -27.5) * mm, "end": v(96.02, 27.5) * mm});
            skLineSegment(sketch, "E57", {"start": v(96.02, 26.78) * mm, "end": v(112.35, 17.36) * mm});
            skLineSegment(sketch, "E58", {"start": v(96.64, 27.86) * mm, "end": v(112.97, 18.43) * mm});
            skLineSegment(sketch, "E59", {"start": v(143.03, -35.79) * mm, "end": v(143.03, -54.64) * mm});
            skLineSegment(sketch, "E60", {"start": v(144.27, -35.79) * mm, "end": v(144.27, -54.64) * mm});
            skLineSegment(sketch, "E61", {"start": v(174.33, 18.43) * mm, "end": v(190.66, 27.86) * mm});
            skLineSegment(sketch, "E62", {"start": v(174.95, 17.36) * mm, "end": v(191.28, 26.78) * mm});
            skLineSegment(sketch, "E63", {"start": v(112.13, 18.2) * mm, "end": v(96.02, -26.08) * mm});
            skLineSegment(sketch, "E64", {"start": v(96.02, -26.08) * mm, "end": v(112.13, 18.2) * mm});
            skLineSegment(sketch, "E65", {"start": v(112.13, 18.2) * mm, "end": v(142.42, 54.3) * mm});
            skLineSegment(sketch, "E66", {"start": v(144.88, 54.3) * mm, "end": v(175.16, 18.2) * mm});
            skLineSegment(sketch, "E67", {"start": v(175.16, 18.2) * mm, "end": v(191.28, -26.08) * mm});
            skLineSegment(sketch, "E68", {"start": v(97.24, -28.2) * mm, "end": v(143.65, -36.4) * mm});
            skLineSegment(sketch, "E69", {"start": v(143.65, -36.4) * mm, "end": v(190.06, -28.2) * mm});
            skLineSegment(sketch, "E70", {"start": v(112.35, 17.36) * mm, "end": v(143.03, -35.79) * mm});
            skLineSegment(sketch, "E71", {"start": v(144.27, -35.79) * mm, "end": v(174.95, 17.36) * mm});
            skLineSegment(sketch, "E72", {"start": v(174.33, 18.43) * mm, "end": v(112.97, 18.43) * mm});
            skCircle(sketch, "E73.cCircle", {"center": v(143.65, 0) * mm, "radius": 35.22 * mm, "construction": true});
            skLineSegment(sketch, "E73.0", {"start": v(143.65, -35.22) * mm, "end": v(113.15, 17.61) * mm});
            skLineSegment(sketch, "E73.1", {"start": v(113.15, 17.61) * mm, "end": v(174.15, 17.61) * mm});
            skLineSegment(sketch, "E73.2", {"start": v(174.15, 17.61) * mm, "end": v(143.65, -35.22) * mm});
            skLineSegment(sketch, "E74", {"start": v(112.89, 17.38) * mm, "end": v(96.7, -27.11) * mm});
            skLineSegment(sketch, "E75", {"start": v(96.7, -27.11) * mm, "end": v(143.32, -35.33) * mm});
            skLineSegment(sketch, "E76", {"start": v(143.98, -35.33) * mm, "end": v(190.6, -27.11) * mm});
            skLineSegment(sketch, "E77", {"start": v(190.6, -27.11) * mm, "end": v(174.41, 17.38) * mm});
            skLineSegment(sketch, "E78", {"start": v(113.21, 17.95) * mm, "end": v(143.65, 54.22) * mm});
            skLineSegment(sketch, "E79", {"start": v(143.65, 54.22) * mm, "end": v(174.09, 17.95) * mm});
            skLineSegment(sketch, "E80", {"start": v(143.65, 0) * mm, "end": v(96.7, -27.11) * mm});
            skLineSegment(sketch, "E81", {"start": v(143.65, 0) * mm, "end": v(143.65, 54.22) * mm});
            skLineSegment(sketch, "E82", {"start": v(143.65, 0) * mm, "end": v(190.6, -27.11) * mm});
            skLineSegment(sketch, "E83", {"start": v(96.53, -26.08) * mm, "end": v(96.53, 27.2) * mm});
            skLineSegment(sketch, "E84", {"start": v(96.53, 27.2) * mm, "end": v(142.68, 53.85) * mm});
            skLineSegment(sketch, "E85", {"start": v(144.62, 53.85) * mm, "end": v(190.77, 27.2) * mm});
            skLineSegment(sketch, "E86", {"start": v(190.77, 27.2) * mm, "end": v(190.77, -26.08) * mm});
            skLineSegment(sketch, "E87", {"start": v(189.8, -27.76) * mm, "end": v(143.65, -54.4) * mm});
            skLineSegment(sketch, "E88", {"start": v(143.65, -54.4) * mm, "end": v(97.5, -27.76) * mm});
            skSolve(sketch);
        }
        {
            var Q0;
            {var subQ0=sQuery(id+"F11.wireOp",EDGE,"E59");var subQ5=sQuery(id+"F11.wireOp",EDGE,"E68");var subQ6=makeQuery(id+"F11.imprint","INTERSECT",VERTEX,{"derivedFrom":[subQ0,subQ5]});Q0=makeQuery(id+"F11.imprint","IMPRINT",FACE,{"disambiguationData":[TD([[makeQuery(id+"F11.imprint","IMPRINT",EDGE,{"disambiguationData":[TD([[subQ6,1.0]])],"derivedFrom":subQ5}),1.0]])]});}
            var Q1;
            {var subQ1=sQuery(id+"F11.wireOp",EDGE,"E46");var subQ9=makeQuery(id+"F11.imprint","INTERSECT",VERTEX,{"derivedFrom":[subQ1,sQuery(id+"F11.wireOp",EDGE,"E88")]});Q1=makeQuery(id+"F11.imprint","IMPRINT",FACE,{"disambiguationData":[TD([[makeQuery(id+"F11.imprint","IMPRINT",EDGE,{"disambiguationData":[TD([[subQ9,1.0]])],"derivedFrom":subQ1}),-1.0]])]});}
            var Q2;
            {var subQ0=sQuery(id+"F11.wireOp",EDGE,"E75");var subQ1=sQuery(id+"F11.wireOp",EDGE,"E41.0");var subQ2=makeQuery(id+"F11.imprint","INTERSECT",VERTEX,{"derivedFrom":[subQ1,subQ0]});Q2=makeQuery(id+"F11.imprint","IMPRINT",FACE,{"disambiguationData":[TD([[makeQuery(id+"F11.imprint","IMPRINT",EDGE,{"disambiguationData":[TD([[subQ2,-1.0]])],"derivedFrom":subQ1}),1.0]])]});}
            var Q3;
            {var subQ0=sQuery(id+"F11.wireOp",EDGE,"E74");var subQ1=sQuery(id+"F11.wireOp",EDGE,"E41.0");var subQ2=makeQuery(id+"F11.imprint","INTERSECT",VERTEX,{"derivedFrom":[subQ1,subQ0]});Q3=makeQuery(id+"F11.imprint","IMPRINT",FACE,{"disambiguationData":[TD([[makeQuery(id+"F11.imprint","IMPRINT",EDGE,{"disambiguationData":[TD([[subQ2,1.0]])],"derivedFrom":subQ1}),1.0]])]});}
            var Q4;
            {var subQ1=sQuery(id+"F11.wireOp",EDGE,"E41.0");var subQ9=makeQuery(id+"F11.imprint","INTERSECT",VERTEX,{"derivedFrom":[subQ1,sQuery(id+"F11.wireOp",EDGE,"E74")]});Q4=makeQuery(id+"F11.imprint","IMPRINT",FACE,{"disambiguationData":[TD([[makeQuery(id+"F11.imprint","IMPRINT",EDGE,{"disambiguationData":[TD([[subQ9,1.0]])],"derivedFrom":subQ1}),-1.0]])]});}
            var Q5;
            {var subQ1=sQuery(id+"F11.wireOp",EDGE,"E41.0");var subQ3=sQuery(id+"F11.wireOp",EDGE,"E74");var subQ4=makeQuery(id+"F11.imprint","INTERSECT",VERTEX,{"derivedFrom":[subQ1,subQ3]});Q5=makeQuery(id+"F11.imprint","IMPRINT",FACE,{"disambiguationData":[TD([[makeQuery(id+"F11.imprint","IMPRINT",EDGE,{"disambiguationData":[TD([[subQ4,-1.0]])],"derivedFrom":subQ3}),-1.0]])]});}
            var Q6;
            {var subQ1=sQuery(id+"F11.wireOp",EDGE,"E41.0");var subQ3=sQuery(id+"F11.wireOp",EDGE,"E75");var subQ4=makeQuery(id+"F11.imprint","INTERSECT",VERTEX,{"derivedFrom":[subQ1,subQ3]});Q6=makeQuery(id+"F11.imprint","IMPRINT",FACE,{"disambiguationData":[TD([[makeQuery(id+"F11.imprint","IMPRINT",EDGE,{"disambiguationData":[TD([[subQ4,1.0]])],"derivedFrom":subQ3}),-1.0]])]});}
            var Q7;
            {var subQ4=sQuery(id+"F11.wireOp",EDGE,"E41.0");var subQ5=makeQuery(id+"F11.imprint","INTERSECT",VERTEX,{"derivedFrom":[subQ4,sQuery(id+"F11.wireOp",EDGE,"E75")]});Q7=makeQuery(id+"F11.imprint","IMPRINT",FACE,{"disambiguationData":[TD([[makeQuery(id+"F11.imprint","IMPRINT",EDGE,{"disambiguationData":[TD([[subQ5,-1.0]])],"derivedFrom":subQ4}),-1.0]])]});}
            var Q8;
            {var subQ3=sQuery(id+"F11.wireOp",EDGE,"E59");var subQ5=sQuery(id+"F11.wireOp",EDGE,"E68");var subQ7=makeQuery(id+"F11.imprint","INTERSECT",VERTEX,{"derivedFrom":[subQ3,subQ5]});Q8=makeQuery(id+"F11.imprint","IMPRINT",FACE,{"disambiguationData":[TD([[makeQuery(id+"F11.imprint","IMPRINT",EDGE,{"disambiguationData":[TD([[subQ7,1.0]])],"derivedFrom":subQ3}),1.0]])]});}
            var Q9;
            {var subQ3=sQuery(id+"F11.wireOp",EDGE,"E60");var subQ5=sQuery(id+"F11.wireOp",EDGE,"E69");var subQ7=makeQuery(id+"F11.imprint","INTERSECT",VERTEX,{"derivedFrom":[subQ3,subQ5]});Q9=makeQuery(id+"F11.imprint","IMPRINT",FACE,{"disambiguationData":[TD([[makeQuery(id+"F11.imprint","IMPRINT",EDGE,{"disambiguationData":[TD([[subQ7,1.0]])],"derivedFrom":subQ3}),-1.0]])]});}
            var Q10;
            {var subQ0=sQuery(id+"F11.wireOp",EDGE,"E76");var subQ1=sQuery(id+"F11.wireOp",EDGE,"E41.2");var subQ2=makeQuery(id+"F11.imprint","INTERSECT",VERTEX,{"derivedFrom":[subQ1,subQ0]});Q10=makeQuery(id+"F11.imprint","IMPRINT",FACE,{"disambiguationData":[TD([[makeQuery(id+"F11.imprint","IMPRINT",EDGE,{"disambiguationData":[TD([[subQ2,1.0]])],"derivedFrom":subQ1}),1.0]])]});}
            var Q11;
            {var subQ1=sQuery(id+"F11.wireOp",EDGE,"E41.2");var subQ3=sQuery(id+"F11.wireOp",EDGE,"E76");var subQ4=makeQuery(id+"F11.imprint","INTERSECT",VERTEX,{"derivedFrom":[subQ1,subQ3]});Q11=makeQuery(id+"F11.imprint","IMPRINT",FACE,{"disambiguationData":[TD([[makeQuery(id+"F11.imprint","IMPRINT",EDGE,{"disambiguationData":[TD([[subQ4,-1.0]])],"derivedFrom":subQ3}),-1.0]])]});}
            var Q12;
            {var subQ1=sQuery(id+"F11.wireOp",EDGE,"E44");var subQ4=makeQuery(id+"F11.imprint","INTERSECT",VERTEX,{"derivedFrom":[subQ1,sQuery(id+"F11.wireOp",EDGE,"E86")]});Q12=makeQuery(id+"F11.imprint","IMPRINT",FACE,{"disambiguationData":[TD([[makeQuery(id+"F11.imprint","IMPRINT",EDGE,{"disambiguationData":[TD([[subQ4,1.0]])],"derivedFrom":subQ1}),-1.0]])]});}
            var Q13;
            {var subQ0=sQuery(id+"F11.wireOp",EDGE,"E60");var subQ5=sQuery(id+"F11.wireOp",EDGE,"E69");var subQ7=makeQuery(id+"F11.imprint","INTERSECT",VERTEX,{"derivedFrom":[subQ0,subQ5]});Q13=makeQuery(id+"F11.imprint","IMPRINT",FACE,{"disambiguationData":[TD([[makeQuery(id+"F11.imprint","IMPRINT",EDGE,{"disambiguationData":[TD([[subQ7,-1.0]])],"derivedFrom":subQ5}),1.0]])]});}
            var Q14;
            {var subQ0=sQuery(id+"F11.wireOp",EDGE,"E54");var subQ5=sQuery(id+"F11.wireOp",EDGE,"E69");var subQ6=makeQuery(id+"F11.imprint","INTERSECT",VERTEX,{"derivedFrom":[subQ0,subQ5]});Q14=makeQuery(id+"F11.imprint","IMPRINT",FACE,{"disambiguationData":[TD([[makeQuery(id+"F11.imprint","IMPRINT",EDGE,{"disambiguationData":[TD([[subQ6,1.0]])],"derivedFrom":subQ5}),1.0]])]});}
            var Q15;
            {var subQ0=sQuery(id+"F11.wireOp",EDGE,"E53");var subQ5=sQuery(id+"F11.wireOp",EDGE,"E67");var subQ6=makeQuery(id+"F11.imprint","INTERSECT",VERTEX,{"derivedFrom":[subQ0,subQ5]});Q15=makeQuery(id+"F11.imprint","IMPRINT",FACE,{"disambiguationData":[TD([[makeQuery(id+"F11.imprint","IMPRINT",EDGE,{"disambiguationData":[TD([[subQ6,1.0]])],"derivedFrom":subQ5}),-1.0]])]});}
            var Q16;
            {var subQ0=sQuery(id+"F11.wireOp",EDGE,"E62");var subQ1=sQuery(id+"F11.wireOp",EDGE,"E53");var subQ2=makeQuery(id+"F11.imprint","INTERSECT",VERTEX,{"derivedFrom":[subQ1,subQ0]});Q16=makeQuery(id+"F11.imprint","IMPRINT",FACE,{"disambiguationData":[TD([[makeQuery(id+"F11.imprint","IMPRINT",EDGE,{"disambiguationData":[TD([[subQ2,-1.0]])],"derivedFrom":subQ1}),-1.0]])]});}
            var Q17;
            {var subQ0=sQuery(id+"F11.wireOp",EDGE,"E62");var subQ5=sQuery(id+"F11.wireOp",EDGE,"E67");var subQ7=makeQuery(id+"F11.imprint","INTERSECT",VERTEX,{"derivedFrom":[subQ0,subQ5]});Q17=makeQuery(id+"F11.imprint","IMPRINT",FACE,{"disambiguationData":[TD([[makeQuery(id+"F11.imprint","IMPRINT",EDGE,{"disambiguationData":[TD([[subQ7,-1.0]])],"derivedFrom":subQ5}),-1.0]])]});}
            var Q18;
            {var subQ0=sQuery(id+"F11.wireOp",EDGE,"E77");var subQ1=sQuery(id+"F11.wireOp",EDGE,"E41.2");var subQ2=makeQuery(id+"F11.imprint","INTERSECT",VERTEX,{"derivedFrom":[subQ1,subQ0]});Q18=makeQuery(id+"F11.imprint","IMPRINT",FACE,{"disambiguationData":[TD([[makeQuery(id+"F11.imprint","IMPRINT",EDGE,{"disambiguationData":[TD([[subQ2,-1.0]])],"derivedFrom":subQ1}),1.0]])]});}
            var Q19;
            {var subQ1=sQuery(id+"F11.wireOp",EDGE,"E41.1");var subQ4=makeQuery(id+"F11.imprint","INTERSECT",VERTEX,{"derivedFrom":[subQ1,sQuery(id+"F11.wireOp",EDGE,"E79")]});Q19=makeQuery(id+"F11.imprint","IMPRINT",FACE,{"disambiguationData":[TD([[makeQuery(id+"F11.imprint","IMPRINT",EDGE,{"disambiguationData":[TD([[subQ4,1.0]])],"derivedFrom":subQ1}),-1.0]])]});}
            var Q20;
            {var subQ0=sQuery(id+"F11.wireOp",EDGE,"E55");var subQ5=sQuery(id+"F11.wireOp",EDGE,"E68");var subQ6=makeQuery(id+"F11.imprint","INTERSECT",VERTEX,{"derivedFrom":[subQ0,subQ5]});Q20=makeQuery(id+"F11.imprint","IMPRINT",FACE,{"disambiguationData":[TD([[makeQuery(id+"F11.imprint","IMPRINT",EDGE,{"disambiguationData":[TD([[subQ6,-1.0]])],"derivedFrom":subQ5}),1.0]])]});}
            var Q21;
            {var subQ0=sQuery(id+"F11.wireOp",EDGE,"E59");var subQ1=sQuery(id+"F11.wireOp",EDGE,"E55");var subQ2=makeQuery(id+"F11.imprint","INTERSECT",VERTEX,{"derivedFrom":[subQ1,subQ0]});Q21=makeQuery(id+"F11.imprint","IMPRINT",FACE,{"disambiguationData":[TD([[makeQuery(id+"F11.imprint","IMPRINT",EDGE,{"disambiguationData":[TD([[subQ2,-1.0]])],"derivedFrom":subQ1}),-1.0]])]});}
            var Q22;
            {var subQ0=sQuery(id+"F11.wireOp",EDGE,"E55");var subQ5=sQuery(id+"F11.wireOp",EDGE,"E59");var subQ6=makeQuery(id+"F11.imprint","INTERSECT",VERTEX,{"derivedFrom":[subQ0,subQ5]});Q22=makeQuery(id+"F11.imprint","IMPRINT",FACE,{"disambiguationData":[TD([[makeQuery(id+"F11.imprint","IMPRINT",EDGE,{"disambiguationData":[TD([[subQ6,1.0]])],"derivedFrom":subQ5}),1.0]])]});}
            var Q23;
            {var subQ0=sQuery(id+"F11.wireOp",EDGE,"E54");var subQ5=sQuery(id+"F11.wireOp",EDGE,"E60");var subQ6=makeQuery(id+"F11.imprint","INTERSECT",VERTEX,{"derivedFrom":[subQ0,subQ5]});Q23=makeQuery(id+"F11.imprint","IMPRINT",FACE,{"disambiguationData":[TD([[makeQuery(id+"F11.imprint","IMPRINT",EDGE,{"disambiguationData":[TD([[subQ6,1.0]])],"derivedFrom":subQ5}),-1.0]])]});}
            var Q24;
            {var subQ0=sQuery(id+"F11.wireOp",EDGE,"E60");var subQ1=sQuery(id+"F11.wireOp",EDGE,"E54");var subQ2=makeQuery(id+"F11.imprint","INTERSECT",VERTEX,{"derivedFrom":[subQ1,subQ0]});Q24=makeQuery(id+"F11.imprint","IMPRINT",FACE,{"disambiguationData":[TD([[makeQuery(id+"F11.imprint","IMPRINT",EDGE,{"disambiguationData":[TD([[subQ2,1.0]])],"derivedFrom":subQ1}),-1.0]])]});}
            var Q25;
            {var subQ0=sQuery(id+"F11.wireOp",EDGE,"E68");var subQ5=sQuery(id+"F11.wireOp",EDGE,"E59");var subQ6=makeQuery(id+"F11.imprint","INTERSECT",VERTEX,{"derivedFrom":[subQ5,subQ0]});Q25=makeQuery(id+"F11.imprint","IMPRINT",FACE,{"disambiguationData":[TD([[makeQuery(id+"F11.imprint","IMPRINT",EDGE,{"disambiguationData":[TD([[subQ6,-1.0]])],"derivedFrom":subQ5}),1.0]])]});}
            var Q26;
            {var subQ0=sQuery(id+"F11.wireOp",EDGE,"E69");var subQ5=sQuery(id+"F11.wireOp",EDGE,"E60");var subQ6=makeQuery(id+"F11.imprint","INTERSECT",VERTEX,{"derivedFrom":[subQ5,subQ0]});Q26=makeQuery(id+"F11.imprint","IMPRINT",FACE,{"disambiguationData":[TD([[makeQuery(id+"F11.imprint","IMPRINT",EDGE,{"disambiguationData":[TD([[subQ6,-1.0]])],"derivedFrom":subQ5}),-1.0]])]});}
            var Q27;
            {var subQ0=sQuery(id+"F11.wireOp",EDGE,"E57");var subQ1=sQuery(id+"F11.wireOp",EDGE,"E56");var subQ2=makeQuery(id+"F11.imprint","INTERSECT",VERTEX,{"derivedFrom":[subQ1,subQ0]});Q27=makeQuery(id+"F11.imprint","IMPRINT",FACE,{"disambiguationData":[TD([[makeQuery(id+"F11.imprint","IMPRINT",EDGE,{"disambiguationData":[TD([[subQ2,1.0]])],"derivedFrom":subQ1}),-1.0]])]});}
            var Q28;
            {var subQ0=sQuery(id+"F11.wireOp",EDGE,"E56");var subQ5=sQuery(id+"F11.wireOp",EDGE,"E64");var subQ7=makeQuery(id+"F11.imprint","INTERSECT",VERTEX,{"derivedFrom":[subQ0,subQ5]});Q28=makeQuery(id+"F11.imprint","IMPRINT",FACE,{"disambiguationData":[TD([[makeQuery(id+"F11.imprint","IMPRINT",EDGE,{"disambiguationData":[TD([[subQ7,-1.0]])],"derivedFrom":subQ5}),-1.0]])]});}
            var Q29;
            {var subQ0=sQuery(id+"F11.wireOp",EDGE,"E57");var subQ5=sQuery(id+"F11.wireOp",EDGE,"E64");var subQ6=makeQuery(id+"F11.imprint","INTERSECT",VERTEX,{"derivedFrom":[subQ0,subQ5]});Q29=makeQuery(id+"F11.imprint","IMPRINT",FACE,{"disambiguationData":[TD([[makeQuery(id+"F11.imprint","IMPRINT",EDGE,{"disambiguationData":[TD([[subQ6,1.0]])],"derivedFrom":subQ5}),-1.0]])]});}
            var Q30;
            {var subQ3=sQuery(id+"F11.wireOp",EDGE,"E83");var subQ5=sQuery(id+"F11.wireOp",EDGE,"E57");var subQ6=makeQuery(id+"F11.imprint","INTERSECT",VERTEX,{"derivedFrom":[subQ5,subQ3]});Q30=makeQuery(id+"F11.imprint","IMPRINT",FACE,{"disambiguationData":[TD([[makeQuery(id+"F11.imprint","IMPRINT",EDGE,{"disambiguationData":[TD([[subQ6,-1.0]])],"derivedFrom":subQ5}),1.0]])]});}
            var Q31;
            {var subQ3=sQuery(id+"F11.wireOp",EDGE,"E84");var subQ5=sQuery(id+"F11.wireOp",EDGE,"E58");var subQ6=makeQuery(id+"F11.imprint","INTERSECT",VERTEX,{"derivedFrom":[subQ5,subQ3]});Q31=makeQuery(id+"F11.imprint","IMPRINT",FACE,{"disambiguationData":[TD([[makeQuery(id+"F11.imprint","IMPRINT",EDGE,{"disambiguationData":[TD([[subQ6,-1.0]])],"derivedFrom":subQ5}),-1.0]])]});}
            var Q32;
            {var subQ3=sQuery(id+"F11.wireOp",EDGE,"E58");var subQ5=sQuery(id+"F11.wireOp",EDGE,"E65");var subQ7=makeQuery(id+"F11.imprint","INTERSECT",VERTEX,{"derivedFrom":[subQ3,subQ5]});Q32=makeQuery(id+"F11.imprint","IMPRINT",FACE,{"disambiguationData":[TD([[makeQuery(id+"F11.imprint","IMPRINT",EDGE,{"disambiguationData":[TD([[subQ7,-1.0]])],"derivedFrom":subQ3}),-1.0]])]});}
            var Q33;
            {var subQ3=sQuery(id+"F11.wireOp",EDGE,"E57");var subQ5=sQuery(id+"F11.wireOp",EDGE,"E64");var subQ7=makeQuery(id+"F11.imprint","INTERSECT",VERTEX,{"derivedFrom":[subQ3,subQ5]});Q33=makeQuery(id+"F11.imprint","IMPRINT",FACE,{"disambiguationData":[TD([[makeQuery(id+"F11.imprint","IMPRINT",EDGE,{"disambiguationData":[TD([[subQ7,-1.0]])],"derivedFrom":subQ3}),1.0]])]});}
            var Q34;
            {var subQ1=sQuery(id+"F11.wireOp",EDGE,"E41.1");var subQ3=sQuery(id+"F11.wireOp",EDGE,"E78");var subQ4=makeQuery(id+"F11.imprint","INTERSECT",VERTEX,{"derivedFrom":[subQ1,subQ3]});Q34=makeQuery(id+"F11.imprint","IMPRINT",FACE,{"disambiguationData":[TD([[makeQuery(id+"F11.imprint","IMPRINT",EDGE,{"disambiguationData":[TD([[subQ4,-1.0]])],"derivedFrom":subQ3}),1.0]])]});}
            var Q35;
            {var subQ0=sQuery(id+"F11.wireOp",EDGE,"E78");var subQ1=sQuery(id+"F11.wireOp",EDGE,"E41.1");var subQ2=makeQuery(id+"F11.imprint","INTERSECT",VERTEX,{"derivedFrom":[subQ1,subQ0]});Q35=makeQuery(id+"F11.imprint","IMPRINT",FACE,{"disambiguationData":[TD([[makeQuery(id+"F11.imprint","IMPRINT",EDGE,{"disambiguationData":[TD([[subQ2,-1.0]])],"derivedFrom":subQ1}),1.0]])]});}
            var Q36;
            {var subQ1=sQuery(id+"F11.wireOp",EDGE,"E42");var subQ11=makeQuery(id+"F11.imprint","INTERSECT",VERTEX,{"derivedFrom":[subQ1,sQuery(id+"F11.wireOp",EDGE,"E84")]});Q36=makeQuery(id+"F11.imprint","IMPRINT",FACE,{"disambiguationData":[TD([[makeQuery(id+"F11.imprint","IMPRINT",EDGE,{"disambiguationData":[TD([[subQ11,1.0]])],"derivedFrom":subQ1}),-1.0]])]});}
            var Q37;
            {var subQ0=sQuery(id+"F11.wireOp",EDGE,"E58");var subQ5=sQuery(id+"F11.wireOp",EDGE,"E65");var subQ7=makeQuery(id+"F11.imprint","INTERSECT",VERTEX,{"derivedFrom":[subQ0,subQ5]});Q37=makeQuery(id+"F11.imprint","IMPRINT",FACE,{"disambiguationData":[TD([[makeQuery(id+"F11.imprint","IMPRINT",EDGE,{"disambiguationData":[TD([[subQ7,-1.0]])],"derivedFrom":subQ5}),-1.0]])]});}
            var Q38;
            {var subQ0=sQuery(id+"F11.wireOp",EDGE,"E56");var subQ5=sQuery(id+"F11.wireOp",EDGE,"E57");var subQ6=makeQuery(id+"F11.imprint","INTERSECT",VERTEX,{"derivedFrom":[subQ0,subQ5]});Q38=makeQuery(id+"F11.imprint","IMPRINT",FACE,{"disambiguationData":[TD([[makeQuery(id+"F11.imprint","IMPRINT",EDGE,{"disambiguationData":[TD([[subQ6,-1.0]])],"derivedFrom":subQ5}),1.0]])]});}
            var Q39;
            {var subQ0=sQuery(id+"F11.wireOp",EDGE,"E51");var subQ5=sQuery(id+"F11.wireOp",EDGE,"E58");var subQ6=makeQuery(id+"F11.imprint","INTERSECT",VERTEX,{"derivedFrom":[subQ0,subQ5]});Q39=makeQuery(id+"F11.imprint","IMPRINT",FACE,{"disambiguationData":[TD([[makeQuery(id+"F11.imprint","IMPRINT",EDGE,{"disambiguationData":[TD([[subQ6,-1.0]])],"derivedFrom":subQ5}),-1.0]])]});}
            var Q40;
            {var subQ0=sQuery(id+"F11.wireOp",EDGE,"E58");var subQ1=sQuery(id+"F11.wireOp",EDGE,"E51");var subQ2=makeQuery(id+"F11.imprint","INTERSECT",VERTEX,{"derivedFrom":[subQ1,subQ0]});Q40=makeQuery(id+"F11.imprint","IMPRINT",FACE,{"disambiguationData":[TD([[makeQuery(id+"F11.imprint","IMPRINT",EDGE,{"disambiguationData":[TD([[subQ2,-1.0]])],"derivedFrom":subQ1}),-1.0]])]});}
            var Q41;
            {var subQ0=sQuery(id+"F11.wireOp",EDGE,"E79");var subQ1=sQuery(id+"F11.wireOp",EDGE,"E41.1");var subQ2=makeQuery(id+"F11.imprint","INTERSECT",VERTEX,{"derivedFrom":[subQ1,subQ0]});Q41=makeQuery(id+"F11.imprint","IMPRINT",FACE,{"disambiguationData":[TD([[makeQuery(id+"F11.imprint","IMPRINT",EDGE,{"disambiguationData":[TD([[subQ2,1.0]])],"derivedFrom":subQ1}),1.0]])]});}
            var Q42;
            {var subQ1=sQuery(id+"F11.wireOp",EDGE,"E41.1");var subQ3=sQuery(id+"F11.wireOp",EDGE,"E79");var subQ4=makeQuery(id+"F11.imprint","INTERSECT",VERTEX,{"derivedFrom":[subQ1,subQ3]});Q42=makeQuery(id+"F11.imprint","IMPRINT",FACE,{"disambiguationData":[TD([[makeQuery(id+"F11.imprint","IMPRINT",EDGE,{"disambiguationData":[TD([[subQ4,1.0]])],"derivedFrom":subQ3}),1.0]])]});}
            var Q43;
            {var subQ3=sQuery(id+"F11.wireOp",EDGE,"E61");var subQ5=sQuery(id+"F11.wireOp",EDGE,"E66");var subQ7=makeQuery(id+"F11.imprint","INTERSECT",VERTEX,{"derivedFrom":[subQ3,subQ5]});Q43=makeQuery(id+"F11.imprint","IMPRINT",FACE,{"disambiguationData":[TD([[makeQuery(id+"F11.imprint","IMPRINT",EDGE,{"disambiguationData":[TD([[subQ7,1.0]])],"derivedFrom":subQ3}),-1.0]])]});}
            var Q44;
            {var subQ3=sQuery(id+"F11.wireOp",EDGE,"E62");var subQ5=sQuery(id+"F11.wireOp",EDGE,"E67");var subQ7=makeQuery(id+"F11.imprint","INTERSECT",VERTEX,{"derivedFrom":[subQ3,subQ5]});Q44=makeQuery(id+"F11.imprint","IMPRINT",FACE,{"disambiguationData":[TD([[makeQuery(id+"F11.imprint","IMPRINT",EDGE,{"disambiguationData":[TD([[subQ7,1.0]])],"derivedFrom":subQ3}),1.0]])]});}
            var Q45;
            {var subQ1=sQuery(id+"F11.wireOp",EDGE,"E41.2");var subQ3=sQuery(id+"F11.wireOp",EDGE,"E77");var subQ4=makeQuery(id+"F11.imprint","INTERSECT",VERTEX,{"derivedFrom":[subQ1,subQ3]});Q45=makeQuery(id+"F11.imprint","IMPRINT",FACE,{"disambiguationData":[TD([[makeQuery(id+"F11.imprint","IMPRINT",EDGE,{"disambiguationData":[TD([[subQ4,1.0]])],"derivedFrom":subQ3}),-1.0]])]});}
            var Q46;
            {var subQ0=sQuery(id+"F11.wireOp",EDGE,"E67");var subQ5=sQuery(id+"F11.wireOp",EDGE,"E62");var subQ6=makeQuery(id+"F11.imprint","INTERSECT",VERTEX,{"derivedFrom":[subQ5,subQ0]});Q46=makeQuery(id+"F11.imprint","IMPRINT",FACE,{"disambiguationData":[TD([[makeQuery(id+"F11.imprint","IMPRINT",EDGE,{"disambiguationData":[TD([[subQ6,-1.0]])],"derivedFrom":subQ5}),1.0]])]});}
            var Q47;
            {var subQ0=sQuery(id+"F11.wireOp",EDGE,"E66");var subQ5=sQuery(id+"F11.wireOp",EDGE,"E61");var subQ6=makeQuery(id+"F11.imprint","INTERSECT",VERTEX,{"derivedFrom":[subQ5,subQ0]});Q47=makeQuery(id+"F11.imprint","IMPRINT",FACE,{"disambiguationData":[TD([[makeQuery(id+"F11.imprint","IMPRINT",EDGE,{"disambiguationData":[TD([[subQ6,-1.0]])],"derivedFrom":subQ5}),-1.0]])]});}
            var Q48;
            {var subQ0=sQuery(id+"F11.wireOp",EDGE,"E61");var subQ5=sQuery(id+"F11.wireOp",EDGE,"E66");var subQ6=makeQuery(id+"F11.imprint","INTERSECT",VERTEX,{"derivedFrom":[subQ0,subQ5]});Q48=makeQuery(id+"F11.imprint","IMPRINT",FACE,{"disambiguationData":[TD([[makeQuery(id+"F11.imprint","IMPRINT",EDGE,{"disambiguationData":[TD([[subQ6,1.0]])],"derivedFrom":subQ5}),-1.0]])]});}
            var Q49;
            {var subQ0=sQuery(id+"F11.wireOp",EDGE,"E61");var subQ1=sQuery(id+"F11.wireOp",EDGE,"E52");var subQ2=makeQuery(id+"F11.imprint","INTERSECT",VERTEX,{"derivedFrom":[subQ1,subQ0]});Q49=makeQuery(id+"F11.imprint","IMPRINT",FACE,{"disambiguationData":[TD([[makeQuery(id+"F11.imprint","IMPRINT",EDGE,{"disambiguationData":[TD([[subQ2,1.0]])],"derivedFrom":subQ1}),-1.0]])]});}
            var Q50;
            {var subQ0=sQuery(id+"F11.wireOp",EDGE,"E52");var subQ5=sQuery(id+"F11.wireOp",EDGE,"E61");var subQ6=makeQuery(id+"F11.imprint","INTERSECT",VERTEX,{"derivedFrom":[subQ0,subQ5]});Q50=makeQuery(id+"F11.imprint","IMPRINT",FACE,{"disambiguationData":[TD([[makeQuery(id+"F11.imprint","IMPRINT",EDGE,{"disambiguationData":[TD([[subQ6,1.0]])],"derivedFrom":subQ5}),-1.0]])]});}
            var Q51;
            {var subQ0=sQuery(id+"F11.wireOp",EDGE,"E53");var subQ5=sQuery(id+"F11.wireOp",EDGE,"E62");var subQ6=makeQuery(id+"F11.imprint","INTERSECT",VERTEX,{"derivedFrom":[subQ0,subQ5]});Q51=makeQuery(id+"F11.imprint","IMPRINT",FACE,{"disambiguationData":[TD([[makeQuery(id+"F11.imprint","IMPRINT",EDGE,{"disambiguationData":[TD([[subQ6,1.0]])],"derivedFrom":subQ5}),1.0]])]});}
            var Q52;
            {var subQ0=sQuery(id+"F11.wireOp",EDGE,"E52");var subQ5=sQuery(id+"F11.wireOp",EDGE,"E66");var subQ6=makeQuery(id+"F11.imprint","INTERSECT",VERTEX,{"derivedFrom":[subQ0,subQ5]});Q52=makeQuery(id+"F11.imprint","IMPRINT",FACE,{"disambiguationData":[TD([[makeQuery(id+"F11.imprint","IMPRINT",EDGE,{"disambiguationData":[TD([[subQ6,-1.0]])],"derivedFrom":subQ5}),-1.0]])]});}
            var Q53;
            {var subQ0=sQuery(id+"F11.wireOp",EDGE,"E51");var subQ5=sQuery(id+"F11.wireOp",EDGE,"E65");var subQ6=makeQuery(id+"F11.imprint","INTERSECT",VERTEX,{"derivedFrom":[subQ0,subQ5]});Q53=makeQuery(id+"F11.imprint","IMPRINT",FACE,{"disambiguationData":[TD([[makeQuery(id+"F11.imprint","IMPRINT",EDGE,{"disambiguationData":[TD([[subQ6,1.0]])],"derivedFrom":subQ5}),-1.0]])]});}
            extrude(context, id + "F12", {"entities" : qUnion([Q0, Q1, Q2, Q3, Q4, Q5, Q6, Q7, Q8, Q9, Q10, Q11, Q12, Q13, Q14, Q15, Q16, Q17, Q18, Q19, Q20, Q21, Q22, Q23, Q24, Q25, Q26, Q27, Q28, Q29, Q30, Q31, Q32, Q33, Q34, Q35, Q36, Q37, Q38, Q39, Q40, Q41, Q42, Q43, Q44, Q45, Q46, Q47, Q48, Q49, Q50, Q51, Q52, Q53]), "oppositeDirection" : true, "depth" : 1.5 * mm});
        }
        {
            var Q0;
            Q0=makeQuery(id+"F12.opExtrude","SWEPT_BODY",BODY,{"disambiguationData":[OSD([sQuery(id+"F11.wireOp",EDGE,"E51"),sQuery(id+"F11.wireOp",EDGE,"E52"),sQuery(id+"F11.wireOp",EDGE,"E53"),sQuery(id+"F11.wireOp",EDGE,"E54"),sQuery(id+"F11.wireOp",EDGE,"E55"),sQuery(id+"F11.wireOp",EDGE,"E56"),sQuery(id+"F11.wireOp",EDGE,"E57"),sQuery(id+"F11.wireOp",EDGE,"E58"),sQuery(id+"F11.wireOp",EDGE,"E59"),sQuery(id+"F11.wireOp",EDGE,"E60"),sQuery(id+"F11.wireOp",EDGE,"E61"),sQuery(id+"F11.wireOp",EDGE,"E62"),sQuery(id+"F11.wireOp",EDGE,"E64"),sQuery(id+"F11.wireOp",EDGE,"E65"),sQuery(id+"F11.wireOp",EDGE,"E66"),sQuery(id+"F11.wireOp",EDGE,"E67"),sQuery(id+"F11.wireOp",EDGE,"E68"),sQuery(id+"F11.wireOp",EDGE,"E69"),sQuery(id+"F11.wireOp",EDGE,"E70"),sQuery(id+"F11.wireOp",EDGE,"E71"),sQuery(id+"F11.wireOp",EDGE,"E72"),sQuery(id+"F11.wireOp",EDGE,"E73.0"),sQuery(id+"F11.wireOp",EDGE,"E73.1"),sQuery(id+"F11.wireOp",EDGE,"E73.2"),sQuery(id+"F11.wireOp",EDGE,"E74"),sQuery(id+"F11.wireOp",EDGE,"E75"),sQuery(id+"F11.wireOp",EDGE,"E76"),sQuery(id+"F11.wireOp",EDGE,"E77"),sQuery(id+"F11.wireOp",EDGE,"E78"),sQuery(id+"F11.wireOp",EDGE,"E79"),sQuery(id+"F11.wireOp",EDGE,"E83"),sQuery(id+"F11.wireOp",EDGE,"E84"),sQuery(id+"F11.wireOp",EDGE,"E85"),sQuery(id+"F11.wireOp",EDGE,"E86"),sQuery(id+"F11.wireOp",EDGE,"E87"),sQuery(id+"F11.wireOp",EDGE,"E88")])]});
            var Q1;
            Q1=makeQuery(id+"F2.opExtrude","SWEPT_BODY",BODY,{"disambiguationData":[OSD([sQuery(id+"F0.wireOp",EDGE,"E26")])]});
            booleanBodies(context, id + "F13", {"operationType" : BooleanOperationType.SUBTRACTION, "tools" : qUnion([Q0]), "targets" : qUnion([Q1])});
        }
        {
            var Q0;
            {var subQ0=sQuery(id+"F0.wireOp",EDGE,"E26");Q0=makeQuery(id+"F13.opBoolean","SPLIT",FACE,{"disambiguationData":[TD([makeQuery(id+"F2.opExtrude","SWEPT_FACE",FACE,{"disambiguationData":[OSD([subQ0])]})])],"derivedFrom":makeQuery(id+"F2.opExtrude","CAP_FACE",FACE,{"disambiguationData":[OSD([subQ0])],"isStart":false})});}
            var Q1;
            Q1=makeQuery(id+"F13.opBoolean","SPLIT",FACE,{"disambiguationData":[TD([makeQuery(id+"F12.opExtrude","SWEPT_FACE",FACE,{"disambiguationData":[OSD([sQuery(id+"F11.wireOp",EDGE,"E58")])]})])],"derivedFrom":makeQuery(id+"F2.opExtrude","CAP_FACE",FACE,{"disambiguationData":[OSD([sQuery(id+"F0.wireOp",EDGE,"E26")])],"isStart":false})});
            var Q2;
            Q2=makeQuery(id+"F13.opBoolean","SPLIT",FACE,{"disambiguationData":[TD([makeQuery(id+"F12.opExtrude","SWEPT_FACE",FACE,{"disambiguationData":[OSD([sQuery(id+"F11.wireOp",EDGE,"E72")])]})])],"derivedFrom":makeQuery(id+"F2.opExtrude","CAP_FACE",FACE,{"disambiguationData":[OSD([sQuery(id+"F0.wireOp",EDGE,"E26")])],"isStart":false})});
            var Q3;
            Q3=makeQuery(id+"F13.opBoolean","SPLIT",FACE,{"disambiguationData":[TD([makeQuery(id+"F12.opExtrude","SWEPT_FACE",FACE,{"disambiguationData":[OSD([sQuery(id+"F11.wireOp",EDGE,"E61")])]})])],"derivedFrom":makeQuery(id+"F2.opExtrude","CAP_FACE",FACE,{"disambiguationData":[OSD([sQuery(id+"F0.wireOp",EDGE,"E26")])],"isStart":false})});
            var Q4;
            Q4=makeQuery(id+"F13.opBoolean","SPLIT",FACE,{"disambiguationData":[TD([makeQuery(id+"F12.opExtrude","SWEPT_FACE",FACE,{"disambiguationData":[OSD([sQuery(id+"F11.wireOp",EDGE,"E62")])]})])],"derivedFrom":makeQuery(id+"F2.opExtrude","CAP_FACE",FACE,{"disambiguationData":[OSD([sQuery(id+"F0.wireOp",EDGE,"E26")])],"isStart":false})});
            var Q5;
            Q5=makeQuery(id+"F13.opBoolean","SPLIT",FACE,{"disambiguationData":[TD([makeQuery(id+"F12.opExtrude","SWEPT_FACE",FACE,{"disambiguationData":[OSD([sQuery(id+"F11.wireOp",EDGE,"E73.0")])]})])],"derivedFrom":makeQuery(id+"F2.opExtrude","CAP_FACE",FACE,{"disambiguationData":[OSD([sQuery(id+"F0.wireOp",EDGE,"E26")])],"isStart":false})});
            var Q6;
            Q6=makeQuery(id+"F13.opBoolean","SPLIT",FACE,{"disambiguationData":[TD([makeQuery(id+"F12.opExtrude","SWEPT_FACE",FACE,{"disambiguationData":[OSD([sQuery(id+"F11.wireOp",EDGE,"E57")])]})])],"derivedFrom":makeQuery(id+"F2.opExtrude","CAP_FACE",FACE,{"disambiguationData":[OSD([sQuery(id+"F0.wireOp",EDGE,"E26")])],"isStart":false})});
            var Q7;
            Q7=makeQuery(id+"F13.opBoolean","SPLIT",FACE,{"disambiguationData":[TD([makeQuery(id+"F12.opExtrude","SWEPT_FACE",FACE,{"disambiguationData":[OSD([sQuery(id+"F11.wireOp",EDGE,"E70")])]})])],"derivedFrom":makeQuery(id+"F2.opExtrude","CAP_FACE",FACE,{"disambiguationData":[OSD([sQuery(id+"F0.wireOp",EDGE,"E26")])],"isStart":false})});
            var Q8;
            Q8=makeQuery(id+"F13.opBoolean","SPLIT",FACE,{"disambiguationData":[TD([makeQuery(id+"F12.opExtrude","SWEPT_FACE",FACE,{"disambiguationData":[OSD([sQuery(id+"F11.wireOp",EDGE,"E71")])]})])],"derivedFrom":makeQuery(id+"F2.opExtrude","CAP_FACE",FACE,{"disambiguationData":[OSD([sQuery(id+"F0.wireOp",EDGE,"E26")])],"isStart":false})});
            var Q9;
            Q9=makeQuery(id+"F13.opBoolean","SPLIT",FACE,{"disambiguationData":[TD([makeQuery(id+"F12.opExtrude","SWEPT_FACE",FACE,{"disambiguationData":[OSD([sQuery(id+"F11.wireOp",EDGE,"E59")])]})])],"derivedFrom":makeQuery(id+"F2.opExtrude","CAP_FACE",FACE,{"disambiguationData":[OSD([sQuery(id+"F0.wireOp",EDGE,"E26")])],"isStart":false})});
            var Q10;
            Q10=makeQuery(id+"F13.opBoolean","SPLIT",FACE,{"disambiguationData":[TD([makeQuery(id+"F12.opExtrude","SWEPT_FACE",FACE,{"disambiguationData":[OSD([sQuery(id+"F11.wireOp",EDGE,"E60")])]})])],"derivedFrom":makeQuery(id+"F2.opExtrude","CAP_FACE",FACE,{"disambiguationData":[OSD([sQuery(id+"F0.wireOp",EDGE,"E26")])],"isStart":false})});
            chamfer(context, id + "F14", {"entities" : qUnion([Q0, Q1, Q2, Q3, Q4, Q5, Q6, Q7, Q8, Q9, Q10]), "chamferType" : ChamferType.TWO_OFFSETS, "width1" : 1.5 * mm, "oppositeDirection" : false, "width2" : 1 * mm, "tangentPropagation" : true});
        }
        {
            var Q0;
            Q0=makeQuery(id+"F1.opExtrude","SWEPT_EDGE",EDGE,{"disambiguationData":[OSD([sQuery(id+"F0.wireOp",EDGE,"E1.2"),sQuery(id+"F0.wireOp",EDGE,"E17")])]});
            var Q1;
            Q1=makeQuery(id+"F1.opExtrude","SWEPT_EDGE",EDGE,{"disambiguationData":[OSD([sQuery(id+"F0.wireOp",EDGE,"E1.3"),sQuery(id+"F0.wireOp",EDGE,"E21")])]});
            var Q2;
            Q2=makeQuery(id+"F1.opExtrude","SWEPT_EDGE",EDGE,{"disambiguationData":[OSD([sQuery(id+"F0.wireOp",EDGE,"E1.4"),sQuery(id+"F0.wireOp",EDGE,"E23")])]});
            var Q3;
            Q3=makeQuery(id+"F1.opExtrude","SWEPT_EDGE",EDGE,{"disambiguationData":[OSD([sQuery(id+"F0.wireOp",EDGE,"E1.1"),sQuery(id+"F0.wireOp",EDGE,"E15")])]});
            var Q4;
            Q4=makeQuery(id+"F1.opExtrude","SWEPT_EDGE",EDGE,{"disambiguationData":[OSD([sQuery(id+"F0.wireOp",EDGE,"E0.5"),sQuery(id+"F0.wireOp",EDGE,"E11")])]});
            var Q5;
            Q5=makeQuery(id+"F1.opExtrude","SWEPT_EDGE",EDGE,{"disambiguationData":[OSD([sQuery(id+"F0.wireOp",EDGE,"E0.0"),sQuery(id+"F0.wireOp",EDGE,"E14")])]});
            var Q6;
            Q6=makeQuery(id+"F1.opExtrude","SWEPT_EDGE",EDGE,{"disambiguationData":[OSD([sQuery(id+"F0.wireOp",EDGE,"E0.6"),sQuery(id+"F0.wireOp",EDGE,"E13")])]});
            var Q7;
            Q7=makeQuery(id+"F1.opExtrude","SWEPT_EDGE",EDGE,{"disambiguationData":[OSD([sQuery(id+"F0.wireOp",EDGE,"E0.1"),sQuery(id+"F0.wireOp",EDGE,"E15")])]});
            var Q8;
            Q8=makeQuery(id+"F1.opExtrude","SWEPT_EDGE",EDGE,{"disambiguationData":[OSD([sQuery(id+"F0.wireOp",EDGE,"E1.3"),sQuery(id+"F0.wireOp",EDGE,"E20")])]});
            var Q9;
            Q9=makeQuery(id+"F1.opExtrude","SWEPT_EDGE",EDGE,{"disambiguationData":[OSD([sQuery(id+"F0.wireOp",EDGE,"E0.0"),sQuery(id+"F0.wireOp",EDGE,"E16")])]});
            var Q10;
            Q10=makeQuery(id+"F1.opExtrude","SWEPT_EDGE",EDGE,{"disambiguationData":[OSD([sQuery(id+"F0.wireOp",EDGE,"E1.6"),sQuery(id+"F0.wireOp",EDGE,"E13")])]});
            var Q11;
            Q11=makeQuery(id+"F1.opExtrude","SWEPT_EDGE",EDGE,{"disambiguationData":[OSD([sQuery(id+"F0.wireOp",EDGE,"E0.1"),sQuery(id+"F0.wireOp",EDGE,"E18")])]});
            var Q12;
            Q12=makeQuery(id+"F1.opExtrude","SWEPT_EDGE",EDGE,{"disambiguationData":[OSD([sQuery(id+"F0.wireOp",EDGE,"E0.2"),sQuery(id+"F0.wireOp",EDGE,"E17")])]});
            var Q13;
            Q13=makeQuery(id+"F1.opExtrude","SWEPT_EDGE",EDGE,{"disambiguationData":[OSD([sQuery(id+"F0.wireOp",EDGE,"E0.3"),sQuery(id+"F0.wireOp",EDGE,"E20")])]});
            var Q14;
            Q14=makeQuery(id+"F1.opExtrude","SWEPT_EDGE",EDGE,{"disambiguationData":[OSD([sQuery(id+"F0.wireOp",EDGE,"E1.5"),sQuery(id+"F0.wireOp",EDGE,"E24")])]});
            var Q15;
            Q15=makeQuery(id+"F1.opExtrude","SWEPT_EDGE",EDGE,{"disambiguationData":[OSD([sQuery(id+"F0.wireOp",EDGE,"E0.6"),sQuery(id+"F0.wireOp",EDGE,"E12")])]});
            var Q16;
            Q16=makeQuery(id+"F1.opExtrude","SWEPT_EDGE",EDGE,{"disambiguationData":[OSD([sQuery(id+"F0.wireOp",EDGE,"E0.5"),sQuery(id+"F0.wireOp",EDGE,"E24")])]});
            var Q17;
            Q17=makeQuery(id+"F1.opExtrude","SWEPT_EDGE",EDGE,{"disambiguationData":[OSD([sQuery(id+"F0.wireOp",EDGE,"E0.4"),sQuery(id+"F0.wireOp",EDGE,"E23")])]});
            var Q18;
            Q18=makeQuery(id+"F1.opExtrude","SWEPT_EDGE",EDGE,{"disambiguationData":[OSD([sQuery(id+"F0.wireOp",EDGE,"E0.3"),sQuery(id+"F0.wireOp",EDGE,"E21")])]});
            var Q19;
            Q19=makeQuery(id+"F1.opExtrude","SWEPT_EDGE",EDGE,{"disambiguationData":[OSD([sQuery(id+"F0.wireOp",EDGE,"E1.6"),sQuery(id+"F0.wireOp",EDGE,"E12")])]});
            var Q20;
            Q20=makeQuery(id+"F1.opExtrude","SWEPT_EDGE",EDGE,{"disambiguationData":[OSD([sQuery(id+"F0.wireOp",EDGE,"E1.0"),sQuery(id+"F0.wireOp",EDGE,"E14")])]});
            var Q21;
            Q21=makeQuery(id+"F1.opExtrude","SWEPT_EDGE",EDGE,{"disambiguationData":[OSD([sQuery(id+"F0.wireOp",EDGE,"E1.0"),sQuery(id+"F0.wireOp",EDGE,"E16")])]});
            var Q22;
            Q22=makeQuery(id+"F1.opExtrude","SWEPT_EDGE",EDGE,{"disambiguationData":[OSD([sQuery(id+"F0.wireOp",EDGE,"E1.2"),sQuery(id+"F0.wireOp",EDGE,"E19")])]});
            var Q23;
            Q23=makeQuery(id+"F1.opExtrude","SWEPT_EDGE",EDGE,{"disambiguationData":[OSD([sQuery(id+"F0.wireOp",EDGE,"E0.4"),sQuery(id+"F0.wireOp",EDGE,"E22")])]});
            var Q24;
            Q24=makeQuery(id+"F1.opExtrude","SWEPT_EDGE",EDGE,{"disambiguationData":[OSD([sQuery(id+"F0.wireOp",EDGE,"E0.2"),sQuery(id+"F0.wireOp",EDGE,"E19")])]});
            var Q25;
            Q25=makeQuery(id+"F1.opExtrude","SWEPT_EDGE",EDGE,{"disambiguationData":[OSD([sQuery(id+"F0.wireOp",EDGE,"E1.4"),sQuery(id+"F0.wireOp",EDGE,"E22")])]});
            fillet(context, id + "F15", {"entities" : qUnion([Q0, Q1, Q2, Q3, Q4, Q5, Q6, Q7, Q8, Q9, Q10, Q11, Q12, Q13, Q14, Q15, Q16, Q17, Q18, Q19, Q20, Q21, Q22, Q23, Q24, Q25]), "radius" : 5 * mm, "tangentPropagation" : true, "allowEdgeOverflow" : false});
        }
        {
            var Q0;
            {var subQ0=sQuery(id+"F0.wireOp",EDGE,"E26");Q0=makeQuery(id+"F14.opChamfer","BLEND_EDGE",EDGE,{"blendedFrom":[makeQuery(id+"F2.opExtrude","CAP_EDGE",EDGE,{"disambiguationData":[OSD([subQ0])],"isStart":false}),makeQuery(id+"F2.opExtrude","SWEPT_FACE",FACE,{"disambiguationData":[OSD([subQ0])]})],"blendedInto":[makeQuery(id+"F2.opExtrude","SWEPT_FACE",FACE,{"disambiguationData":[OSD([subQ0])]})]});}
            var Q1;
            Q1=makeQuery(id+"F2.opExtrude","CAP_EDGE",EDGE,{"disambiguationData":[OSD([sQuery(id+"F0.wireOp",EDGE,"E2")])],"isStart":false});
            chamfer(context, id + "F16", {"entities" : qUnion([Q0, Q1]), "width" : 3 * mm, "tangentPropagation" : true});
        }
    });
